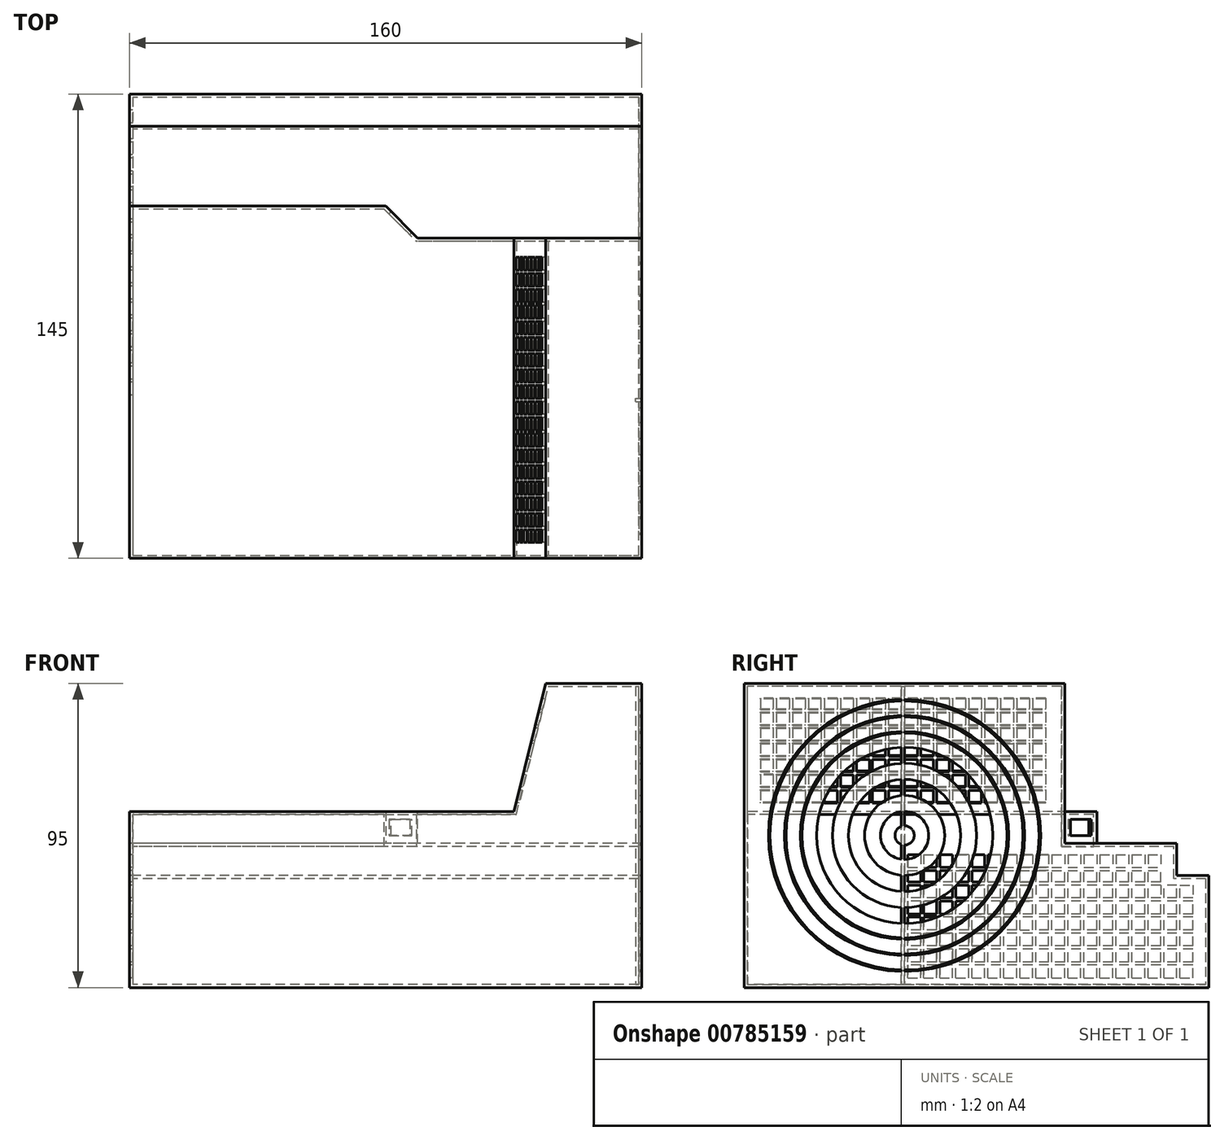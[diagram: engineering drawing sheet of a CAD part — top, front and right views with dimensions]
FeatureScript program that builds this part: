
annotation { "Feature Type Name" : "Feature", "Feature Type Description" : "" }
export const myFeature = defineFeature(function(context is Context, id is Id, definition is map)
    precondition{}
    {
        {
            var Q0;
            Q0=qCreatedBy(makeId("Top.planeOp"),FACE);
            var sketch = newSketch(context, id + "F0", { "sketchPlane" : qUnion([Q0])});
            skLineSegment(sketch, "E0", {"start": v(0, 0) * mm, "end": v(160, 0) * mm});
            skLineSegment(sketch, "E1", {"start": v(160, 0) * mm, "end": v(160, 145) * mm});
            skLineSegment(sketch, "E2", {"start": v(160, 145) * mm, "end": v(0, 145) * mm});
            skLineSegment(sketch, "E3", {"start": v(0, 145) * mm, "end": v(0, 0) * mm});
            skSolve(sketch);
        }
        {
            var Q0;
            Q0=qSketchRegion(id+"F0",true);
            extrude(context, id + "F1", {"entities" : qUnion([Q0]), "depth" : 55 * mm, "offsetDistance" : 25 * mm});
        }
        {
            var Q0;
            Q0=makeQuery(id+"F1.opExtrude","SWEPT_FACE",FACE,{"disambiguationData":[OSD([sQuery(id+"F0.wireOp",EDGE,"E3")])]});
            var sketch = newSketch(context, id + "F2", { "sketchPlane" : qUnion([Q0])});
            skLineSegment(sketch, "E4", {"start": v(-145, 0) * mm, "end": v(-145, 35) * mm});
            skLineSegment(sketch, "E5", {"start": v(-145, 35) * mm, "end": v(-135, 35) * mm});
            skLineSegment(sketch, "E6", {"start": v(-135, 35) * mm, "end": v(-135, 45) * mm});
            skLineSegment(sketch, "E7", {"start": v(-135, 45) * mm, "end": v(-100, 45) * mm});
            skLineSegment(sketch, "E8", {"start": v(-100, 45) * mm, "end": v(-100, 55) * mm});
            skLineSegment(sketch, "E9", {"start": v(-100, 55) * mm, "end": v(-145, 55) * mm});
            skLineSegment(sketch, "E10", {"start": v(-145, 55) * mm, "end": v(-145, 35) * mm});
            skSolve(sketch);
        }
        {
            var Q0;
            Q0=qSketchRegion(id+"F2",true);
            extrude(context, id + "F3", {"entities" : qUnion([Q0]), "operationType" : NewBodyOperationType.REMOVE, "oppositeDirection" : true, "depth" : 165 * mm, "offsetDistance" : 25 * mm});
        }
        {
            var Q0;
            Q0=makeQuery(id+"F1.opExtrude","SWEPT_FACE",FACE,{"disambiguationData":[OSD([sQuery(id+"F0.wireOp",EDGE,"E0")])]});
            var sketch = newSketch(context, id + "F4", { "sketchPlane" : qUnion([Q0])});
            skLineSegment(sketch, "E11", {"start": v(160, 55) * mm, "end": v(120, 55) * mm});
            skLineSegment(sketch, "E12", {"start": v(160, 55) * mm, "end": v(160, 95) * mm});
            skLineSegment(sketch, "E13", {"start": v(160, 95) * mm, "end": v(130, 95) * mm});
            skLineSegment(sketch, "E14", {"start": v(130, 95) * mm, "end": v(120, 55) * mm});
            skSolve(sketch);
        }
        {
            var Q0;
            Q0=qSketchRegion(id+"F4",true);
            extrude(context, id + "F5", {"entities" : qUnion([Q0]), "operationType" : NewBodyOperationType.ADD, "oppositeDirection" : true, "depth" : 100 * mm, "offsetDistance" : 25 * mm});
        }
        {
            var Q0;
            Q0=makeQuery(id+"F1.opExtrude","SWEPT_FACE",FACE,{"disambiguationData":[OSD([sQuery(id+"F0.wireOp",EDGE,"E3")])]});
            var sketch = newSketch(context, id + "F6", { "sketchPlane" : qUnion([Q0])});
            skLineSegment(sketch, "E15.bottom", {"start": v(-100, 45) * mm, "end": v(-110, 45) * mm});
            skLineSegment(sketch, "E15.top", {"start": v(-100, 55) * mm, "end": v(-110, 55) * mm});
            skLineSegment(sketch, "E15.left", {"start": v(-100, 45) * mm, "end": v(-100, 55) * mm});
            skLineSegment(sketch, "E15.right", {"start": v(-110, 45) * mm, "end": v(-110, 55) * mm});
            skSolve(sketch);
        }
        {
            var Q0;
            Q0=qSketchRegion(id+"F6",true);
            extrude(context, id + "F7", {"entities" : qUnion([Q0]), "operationType" : NewBodyOperationType.ADD, "oppositeDirection" : true, "depth" : 90 * mm, "offsetDistance" : 25 * mm});
        }
        {
            var Q0;
            Q0=makeQuery(id+"F7.opExtrude","CAP_EDGE",EDGE,{"disambiguationData":[OSD([sQuery(id+"F6.wireOp",EDGE,"E15.right")])],"isStart":false});
            chamfer(context, id + "F8", {"entities" : qUnion([Q0]), "width" : 10 * mm, "tangentPropagation" : true});
        }
        {
            var Q0;
            Q0=makeQuery(id+"F5.boolean.opBoolean","MERGE",FACE,{"derivedFrom":[makeQuery(id+"F1.opExtrude","SWEPT_FACE",FACE,{"disambiguationData":[OSD([sQuery(id+"F0.wireOp",EDGE,"E0")])]}),makeQuery(id+"F5.opExtrude","CAP_FACE",FACE,{"disambiguationData":[OSD([sQuery(id+"F4.wireOp",EDGE,"E11"),sQuery(id+"F4.wireOp",EDGE,"E12"),sQuery(id+"F4.wireOp",EDGE,"E13"),sQuery(id+"F4.wireOp",EDGE,"E14")])],"isStart":true})]});
            shell(context, id + "F9", {"entities" : qUnion([Q0]), "thickness" : 1 * mm});
        }
        {
            var Q0;
            Q0=makeQuery(id+"F5.opExtrude","SWEPT_FACE",FACE,{"disambiguationData":[OSD([sQuery(id+"F4.wireOp",EDGE,"E14")])]});
            var sketch = newSketch(context, id + "F10", { "sketchPlane" : qUnion([Q0])});
            skLineSegment(sketch, "E16", {"start": v(-94.5, 119.96) * mm, "end": v(-94, 119.96) * mm});
            skLineSegment(sketch, "E17", {"start": v(-89.5, 119.96) * mm, "end": v(-89, 119.96) * mm});
            skLineSegment(sketch, "E18", {"start": v(-4.5, 115.46) * mm, "end": v(-4.5, 114.96) * mm});
            skLineSegment(sketch, "E19", {"start": v(-4.5, 104.96) * mm, "end": v(-4.5, 104.46) * mm});
            skLineSegment(sketch, "E20", {"start": v(-4.5, 99.96) * mm, "end": v(-4.5, 99.46) * mm});
            skLineSegment(sketch, "E21", {"start": v(-4.5, 94.96) * mm, "end": v(-4.5, 94.46) * mm});
            skLineSegment(sketch, "E22.0", {"start": v(-90, 118.96) * mm, "end": v(-90, 115.46) * mm});
            skLineSegment(sketch, "E23.0", {"start": v(-89, 118.96) * mm, "end": v(-89, 115.46) * mm});
            skLineSegment(sketch, "E24.0", {"start": v(-94, 118.96) * mm, "end": v(-94, 115.46) * mm});
            skLineSegment(sketch, "E25.0", {"start": v(-94, 85.46) * mm, "end": v(-90, 85.46) * mm});
            skLineSegment(sketch, "E26.0", {"start": v(-5, 90.46) * mm, "end": v(-9, 90.46) * mm});
            skLineSegment(sketch, "E27.0", {"start": v(-5, 89.46) * mm, "end": v(-9, 89.46) * mm});
            skLineSegment(sketch, "E28.0", {"start": v(-5, 95.46) * mm, "end": v(-9, 95.46) * mm});
            skLineSegment(sketch, "E29.0", {"start": v(-5, 100.46) * mm, "end": v(-9, 100.46) * mm});
            skLineSegment(sketch, "E30.0", {"start": v(-5, 99.46) * mm, "end": v(-9, 99.46) * mm});
            skLineSegment(sketch, "E31.0", {"start": v(-5, 105.46) * mm, "end": v(-9, 105.46) * mm});
            skLineSegment(sketch, "E32.0", {"start": v(-5, 104.46) * mm, "end": v(-9, 104.46) * mm});
            skLineSegment(sketch, "E33.0", {"start": v(-5, 110.46) * mm, "end": v(-9, 110.46) * mm});
            skLineSegment(sketch, "E34.0", {"start": v(-5, 109.46) * mm, "end": v(-9, 109.46) * mm});
            skLineSegment(sketch, "E35.0", {"start": v(-5, 115.46) * mm, "end": v(-9, 115.46) * mm});
            skLineSegment(sketch, "E36.0", {"start": v(-5, 114.46) * mm, "end": v(-9, 114.46) * mm});
            skLineSegment(sketch, "E37.0", {"start": v(-85, 118.96) * mm, "end": v(-85, 115.46) * mm});
            skLineSegment(sketch, "E38.0", {"start": v(-84, 118.96) * mm, "end": v(-84, 115.46) * mm});
            skLineSegment(sketch, "E39.0", {"start": v(-80, 118.96) * mm, "end": v(-80, 115.46) * mm});
            skLineSegment(sketch, "E40.0", {"start": v(-75, 118.96) * mm, "end": v(-75, 115.46) * mm});
            skLineSegment(sketch, "E41.0", {"start": v(-74, 118.96) * mm, "end": v(-74, 115.46) * mm});
            skLineSegment(sketch, "E42.0", {"start": v(-70, 118.96) * mm, "end": v(-70, 115.46) * mm});
            skLineSegment(sketch, "E43.0", {"start": v(-69, 118.96) * mm, "end": v(-69, 115.46) * mm});
            skLineSegment(sketch, "E44.0", {"start": v(-65, 118.96) * mm, "end": v(-65, 115.46) * mm});
            skLineSegment(sketch, "E45.0", {"start": v(-64, 118.96) * mm, "end": v(-64, 115.46) * mm});
            skLineSegment(sketch, "E46.0", {"start": v(-60, 118.96) * mm, "end": v(-60, 115.46) * mm});
            skLineSegment(sketch, "E47.0", {"start": v(-59, 118.96) * mm, "end": v(-59, 115.46) * mm});
            skLineSegment(sketch, "E48.0", {"start": v(-55, 118.96) * mm, "end": v(-55, 115.46) * mm});
            skLineSegment(sketch, "E49.0", {"start": v(-54, 118.96) * mm, "end": v(-54, 115.46) * mm});
            skLineSegment(sketch, "E50.0", {"start": v(-50, 118.96) * mm, "end": v(-50, 115.46) * mm});
            skLineSegment(sketch, "E51.0", {"start": v(-49, 118.96) * mm, "end": v(-49, 115.46) * mm});
            skLineSegment(sketch, "E52.0", {"start": v(-45, 118.96) * mm, "end": v(-45, 115.46) * mm});
            skLineSegment(sketch, "E53.0", {"start": v(-44, 118.96) * mm, "end": v(-44, 115.46) * mm});
            skLineSegment(sketch, "E54.0", {"start": v(-40, 118.96) * mm, "end": v(-40, 115.46) * mm});
            skLineSegment(sketch, "E55.0", {"start": v(-39, 118.96) * mm, "end": v(-39, 115.46) * mm});
            skLineSegment(sketch, "E56.0", {"start": v(-35, 118.96) * mm, "end": v(-35, 115.46) * mm});
            skLineSegment(sketch, "E57.0", {"start": v(-34, 118.96) * mm, "end": v(-34, 115.46) * mm});
            skLineSegment(sketch, "E58.0", {"start": v(-30, 118.96) * mm, "end": v(-30, 115.46) * mm});
            skLineSegment(sketch, "E59.0", {"start": v(-29, 118.96) * mm, "end": v(-29, 115.46) * mm});
            skLineSegment(sketch, "E60.0", {"start": v(-19, 118.96) * mm, "end": v(-19, 115.46) * mm});
            skLineSegment(sketch, "E61.0", {"start": v(-15, 118.96) * mm, "end": v(-15, 115.46) * mm});
            skLineSegment(sketch, "E62.0", {"start": v(-14, 118.96) * mm, "end": v(-14, 115.46) * mm});
            skLineSegment(sketch, "E63.0", {"start": v(-9, 118.96) * mm, "end": v(-9, 115.46) * mm});
            skLineSegment(sketch, "E64.trimOffspring", {"start": v(-4.5, 105.46) * mm, "end": v(-4.5, 104.96) * mm});
            skLineSegment(sketch, "E65.trimOffspring", {"start": v(-4.5, 100.46) * mm, "end": v(-4.5, 99.96) * mm});
            skLineSegment(sketch, "E66.trimOffspring", {"start": v(-4.5, 95.46) * mm, "end": v(-4.5, 94.96) * mm});
            skLineSegment(sketch, "E67.0", {"start": v(-5, 118.96) * mm, "end": v(-5, 115.46) * mm});
            skLineSegment(sketch, "E68.trimOffspring", {"start": v(-85, 119.96) * mm, "end": v(-84.5, 119.96) * mm});
            skLineSegment(sketch, "E69.trimOffspring", {"start": v(-90, 119.96) * mm, "end": v(-89.5, 119.96) * mm});
            skLineSegment(sketch, "E70.trimOffspring", {"start": v(-94, 119.96) * mm, "end": v(-94.5, 119.96) * mm});
            skLineSegment(sketch, "E71.trimOffspring", {"start": v(-89, 119.96) * mm, "end": v(-90, 119.96) * mm});
            skLineSegment(sketch, "E72.0", {"start": v(-94, 118.96) * mm, "end": v(-90, 118.96) * mm});
            skPoint(sketch, "E73.trimOffspring.end.orphan", {"position": v(-98.93, 117.24) * mm});
            skLineSegment(sketch, "E74.trimOffspring", {"start": v(-94, 114.46) * mm, "end": v(-94, 110.46) * mm});
            skLineSegment(sketch, "E75.trimOffspring", {"start": v(-89, 118.96) * mm, "end": v(-85, 118.96) * mm});
            skLineSegment(sketch, "E76.trimOffspring", {"start": v(-84, 118.96) * mm, "end": v(-80, 118.96) * mm});
            skLineSegment(sketch, "E77.trimOffspring", {"start": v(-79, 118.96) * mm, "end": v(-75, 118.96) * mm});
            skLineSegment(sketch, "E78.trimOffspring", {"start": v(-75, 115.46) * mm, "end": v(-79, 115.46) * mm});
            skLineSegment(sketch, "E79.trimOffspring", {"start": v(-74, 114.46) * mm, "end": v(-74, 110.46) * mm});
            skLineSegment(sketch, "E80.trimOffspring", {"start": v(-75, 114.46) * mm, "end": v(-75, 110.46) * mm});
            skLineSegment(sketch, "E81.trimOffspring", {"start": v(-75, 114.46) * mm, "end": v(-79, 114.46) * mm});
            skLineSegment(sketch, "E82.trimOffspring", {"start": v(-79, 114.46) * mm, "end": v(-79, 110.46) * mm});
            skLineSegment(sketch, "E83.trimOffspring", {"start": v(-80, 114.46) * mm, "end": v(-80, 110.46) * mm});
            skLineSegment(sketch, "E84.trimOffspring", {"start": v(-80, 114.46) * mm, "end": v(-84, 114.46) * mm});
            skLineSegment(sketch, "E85.trimOffspring", {"start": v(-74, 118.96) * mm, "end": v(-70, 118.96) * mm});
            skLineSegment(sketch, "E86.trimOffspring", {"start": v(-69, 118.96) * mm, "end": v(-65, 118.96) * mm});
            skLineSegment(sketch, "E87", {"start": v(-79, 118.96) * mm, "end": v(-80, 118.96) * mm});
            skLineSegment(sketch, "E88.trimOffspring", {"start": v(-85, 115.46) * mm, "end": v(-89, 115.46) * mm});
            skLineSegment(sketch, "E89.trimOffspring", {"start": v(-84, 114.46) * mm, "end": v(-84, 110.46) * mm});
            skLineSegment(sketch, "E90.trimOffspring", {"start": v(-85, 114.46) * mm, "end": v(-85, 110.46) * mm});
            skLineSegment(sketch, "E91.trimOffspring", {"start": v(-85, 114.46) * mm, "end": v(-89, 114.46) * mm});
            skLineSegment(sketch, "E92.trimOffspring", {"start": v(-85, 110.46) * mm, "end": v(-89, 110.46) * mm});
            skLineSegment(sketch, "E93.trimOffspring", {"start": v(-84, 109.46) * mm, "end": v(-84, 105.46) * mm});
            skLineSegment(sketch, "E94.trimOffspring", {"start": v(-85, 109.46) * mm, "end": v(-85, 105.46) * mm});
            skLineSegment(sketch, "E95.trimOffspring", {"start": v(-85, 109.46) * mm, "end": v(-89, 109.46) * mm});
            skLineSegment(sketch, "E96.trimOffspring", {"start": v(-90, 109.46) * mm, "end": v(-90, 105.46) * mm});
            skLineSegment(sketch, "E97.trimOffspring", {"start": v(-89, 109.46) * mm, "end": v(-89, 105.46) * mm});
            skLineSegment(sketch, "E98.trimOffspring", {"start": v(-90, 110.46) * mm, "end": v(-94, 110.46) * mm});
            skLineSegment(sketch, "E99.trimOffspring", {"start": v(-90, 109.46) * mm, "end": v(-94, 109.46) * mm});
            skLineSegment(sketch, "E100.trimOffspring", {"start": v(-90, 114.46) * mm, "end": v(-94, 114.46) * mm});
            skLineSegment(sketch, "E101.trimOffspring", {"start": v(-89, 114.46) * mm, "end": v(-89, 110.46) * mm});
            skLineSegment(sketch, "E102.trimOffspring", {"start": v(-90, 114.46) * mm, "end": v(-90, 110.46) * mm});
            skLineSegment(sketch, "E103.trimOffspring", {"start": v(-90, 115.46) * mm, "end": v(-94, 115.46) * mm});
            skLineSegment(sketch, "E104.trimOffspring", {"start": v(-80, 109.46) * mm, "end": v(-80, 105.46) * mm});
            skLineSegment(sketch, "E105.trimOffspring", {"start": v(-80, 110.46) * mm, "end": v(-84, 110.46) * mm});
            skLineSegment(sketch, "E106.trimOffspring", {"start": v(-79, 109.46) * mm, "end": v(-79, 105.46) * mm});
            skLineSegment(sketch, "E107.trimOffspring", {"start": v(-80, 109.46) * mm, "end": v(-84, 109.46) * mm});
            skLineSegment(sketch, "E108.trimOffspring", {"start": v(-75, 109.46) * mm, "end": v(-79, 109.46) * mm});
            skLineSegment(sketch, "E109.trimOffspring", {"start": v(-74, 109.46) * mm, "end": v(-74, 105.46) * mm});
            skLineSegment(sketch, "E110.trimOffspring", {"start": v(-75, 109.46) * mm, "end": v(-75, 105.46) * mm});
            skLineSegment(sketch, "E111.trimOffspring", {"start": v(-75, 110.46) * mm, "end": v(-79, 110.46) * mm});
            skLineSegment(sketch, "E112.trimOffspring", {"start": v(-70, 109.46) * mm, "end": v(-70, 105.46) * mm});
            skLineSegment(sketch, "E113.trimOffspring", {"start": v(-70, 110.46) * mm, "end": v(-74, 110.46) * mm});
            skLineSegment(sketch, "E114.trimOffspring", {"start": v(-69, 109.46) * mm, "end": v(-69, 105.46) * mm});
            skLineSegment(sketch, "E115.trimOffspring", {"start": v(-70, 109.46) * mm, "end": v(-74, 109.46) * mm});
            skLineSegment(sketch, "E116.trimOffspring", {"start": v(-70, 114.46) * mm, "end": v(-74, 114.46) * mm});
            skLineSegment(sketch, "E117.trimOffspring", {"start": v(-70, 114.46) * mm, "end": v(-70, 110.46) * mm});
            skLineSegment(sketch, "E118.trimOffspring", {"start": v(-70, 115.46) * mm, "end": v(-74, 115.46) * mm});
            skLineSegment(sketch, "E119.trimOffspring", {"start": v(-69, 114.46) * mm, "end": v(-69, 110.46) * mm});
            skLineSegment(sketch, "E120.trimOffspring", {"start": v(-65, 114.46) * mm, "end": v(-65, 110.46) * mm});
            skLineSegment(sketch, "E121.trimOffspring", {"start": v(-65, 115.46) * mm, "end": v(-69, 115.46) * mm});
            skLineSegment(sketch, "E122.trimOffspring", {"start": v(-64, 118.96) * mm, "end": v(-60, 118.96) * mm});
            skLineSegment(sketch, "E123.trimOffspring", {"start": v(-65, 114.46) * mm, "end": v(-69, 114.46) * mm});
            skLineSegment(sketch, "E124.trimOffspring", {"start": v(-64, 114.46) * mm, "end": v(-64, 110.46) * mm});
            skLineSegment(sketch, "E125.trimOffspring", {"start": v(-59, 118.96) * mm, "end": v(-55, 118.96) * mm});
            skLineSegment(sketch, "E126.trimOffspring", {"start": v(-60, 115.46) * mm, "end": v(-64, 115.46) * mm});
            skLineSegment(sketch, "E127.trimOffspring", {"start": v(-60, 114.46) * mm, "end": v(-60, 110.46) * mm});
            skLineSegment(sketch, "E128.trimOffspring", {"start": v(-60, 114.46) * mm, "end": v(-64, 114.46) * mm});
            skLineSegment(sketch, "E129.trimOffspring", {"start": v(-59, 114.46) * mm, "end": v(-59, 110.46) * mm});
            skLineSegment(sketch, "E130.trimOffspring", {"start": v(-60, 110.46) * mm, "end": v(-64, 110.46) * mm});
            skLineSegment(sketch, "E131.trimOffspring", {"start": v(-60, 109.46) * mm, "end": v(-60, 105.46) * mm});
            skLineSegment(sketch, "E132.trimOffspring", {"start": v(-60, 109.46) * mm, "end": v(-64, 109.46) * mm});
            skLineSegment(sketch, "E133.trimOffspring", {"start": v(-59, 109.46) * mm, "end": v(-59, 105.46) * mm});
            skLineSegment(sketch, "E134.trimOffspring", {"start": v(-64, 109.46) * mm, "end": v(-64, 105.46) * mm});
            skLineSegment(sketch, "E135.trimOffspring", {"start": v(-65, 110.46) * mm, "end": v(-69, 110.46) * mm});
            skLineSegment(sketch, "E136.trimOffspring", {"start": v(-65, 109.46) * mm, "end": v(-65, 105.46) * mm});
            skLineSegment(sketch, "E137.trimOffspring", {"start": v(-65, 109.46) * mm, "end": v(-69, 109.46) * mm});
            skLineSegment(sketch, "E138.trimOffspring", {"start": v(-94, 109.46) * mm, "end": v(-94, 105.46) * mm});
            skLineSegment(sketch, "E139.trimOffspring", {"start": v(-94, 99.46) * mm, "end": v(-94, 95.46) * mm});
            skLineSegment(sketch, "E140.trimOffspring", {"start": v(-90, 99.46) * mm, "end": v(-90, 95.46) * mm});
            skLineSegment(sketch, "E141.trimOffspring", {"start": v(-90, 100.46) * mm, "end": v(-94, 100.46) * mm});
            skLineSegment(sketch, "E142.trimOffspring", {"start": v(-89, 99.46) * mm, "end": v(-89, 95.46) * mm});
            skLineSegment(sketch, "E143.trimOffspring", {"start": v(-90, 99.46) * mm, "end": v(-94, 99.46) * mm});
            skLineSegment(sketch, "E144.trimOffspring", {"start": v(-90, 104.46) * mm, "end": v(-94, 104.46) * mm});
            skLineSegment(sketch, "E145.trimOffspring", {"start": v(-90, 104.46) * mm, "end": v(-90, 100.46) * mm});
            skLineSegment(sketch, "E146.trimOffspring", {"start": v(-90, 105.46) * mm, "end": v(-94, 105.46) * mm});
            skLineSegment(sketch, "E147.trimOffspring", {"start": v(-89, 104.46) * mm, "end": v(-89, 100.46) * mm});
            skLineSegment(sketch, "E148.trimOffspring", {"start": v(-84, 104.46) * mm, "end": v(-84, 100.46) * mm});
            skLineSegment(sketch, "E149.trimOffspring", {"start": v(-85, 105.46) * mm, "end": v(-89, 105.46) * mm});
            skLineSegment(sketch, "E150.trimOffspring", {"start": v(-85, 104.46) * mm, "end": v(-85, 100.46) * mm});
            skLineSegment(sketch, "E151.trimOffspring", {"start": v(-85, 104.46) * mm, "end": v(-89, 104.46) * mm});
            skLineSegment(sketch, "E152.trimOffspring", {"start": v(-80, 104.46) * mm, "end": v(-80, 100.46) * mm});
            skLineSegment(sketch, "E153.trimOffspring", {"start": v(-80, 105.46) * mm, "end": v(-84, 105.46) * mm});
            skLineSegment(sketch, "E154.trimOffspring", {"start": v(-79, 104.46) * mm, "end": v(-79, 100.46) * mm});
            skLineSegment(sketch, "E155.trimOffspring", {"start": v(-80, 104.46) * mm, "end": v(-84, 104.46) * mm});
            skLineSegment(sketch, "E156", {"start": v(-79, 118.96) * mm, "end": v(-79, 115.46) * mm});
            skLineSegment(sketch, "E157.trimOffspring", {"start": v(-80, 115.46) * mm, "end": v(-84, 115.46) * mm});
            skLineSegment(sketch, "E158.trimOffspring", {"start": v(-70, 105.46) * mm, "end": v(-74, 105.46) * mm});
            skLineSegment(sketch, "E159.trimOffspring", {"start": v(-70, 104.46) * mm, "end": v(-74, 104.46) * mm});
            skLineSegment(sketch, "E160.trimOffspring", {"start": v(-69, 104.46) * mm, "end": v(-69, 100.46) * mm});
            skLineSegment(sketch, "E161.trimOffspring", {"start": v(-70, 104.46) * mm, "end": v(-70, 100.46) * mm});
            skLineSegment(sketch, "E162.trimOffspring", {"start": v(-74, 104.46) * mm, "end": v(-74, 100.46) * mm});
            skLineSegment(sketch, "E163.trimOffspring", {"start": v(-75, 104.46) * mm, "end": v(-79, 104.46) * mm});
            skLineSegment(sketch, "E164.trimOffspring", {"start": v(-75, 104.46) * mm, "end": v(-75, 100.46) * mm});
            skLineSegment(sketch, "E165.trimOffspring", {"start": v(-75, 105.46) * mm, "end": v(-79, 105.46) * mm});
            skLineSegment(sketch, "E166.trimOffspring", {"start": v(-94, 94.46) * mm, "end": v(-94, 90.46) * mm});
            skLineSegment(sketch, "E167.trimOffspring", {"start": v(-90, 94.46) * mm, "end": v(-90, 90.46) * mm});
            skLineSegment(sketch, "E168.trimOffspring", {"start": v(-89, 94.46) * mm, "end": v(-89, 90.46) * mm});
            skLineSegment(sketch, "E169.trimOffspring", {"start": v(-90, 95.46) * mm, "end": v(-94, 95.46) * mm});
            skLineSegment(sketch, "E170.trimOffspring", {"start": v(-94, 89.46) * mm, "end": v(-94, 85.46) * mm});
            skLineSegment(sketch, "E171.trimOffspring", {"start": v(-89, 85.46) * mm, "end": v(-85, 85.46) * mm});
            skLineSegment(sketch, "E172.trimOffspring", {"start": v(-90, 89.46) * mm, "end": v(-94, 89.46) * mm});
            skLineSegment(sketch, "E173.trimOffspring", {"start": v(-90, 90.46) * mm, "end": v(-94, 90.46) * mm});
            skLineSegment(sketch, "E174.trimOffspring", {"start": v(-90, 89.46) * mm, "end": v(-90, 85.46) * mm});
            skLineSegment(sketch, "E175.trimOffspring", {"start": v(-89, 89.46) * mm, "end": v(-89, 85.46) * mm});
            skLineSegment(sketch, "E176.trimOffspring", {"start": v(-90, 94.46) * mm, "end": v(-94, 94.46) * mm});
            skLineSegment(sketch, "E177.trimOffspring", {"start": v(-85, 94.46) * mm, "end": v(-89, 94.46) * mm});
            skLineSegment(sketch, "E178.trimOffspring", {"start": v(-85, 94.46) * mm, "end": v(-85, 90.46) * mm});
            skLineSegment(sketch, "E179.trimOffspring", {"start": v(-85, 95.46) * mm, "end": v(-89, 95.46) * mm});
            skLineSegment(sketch, "E180.trimOffspring", {"start": v(-84, 94.46) * mm, "end": v(-84, 90.46) * mm});
            skLineSegment(sketch, "E181.trimOffspring", {"start": v(-85, 99.46) * mm, "end": v(-89, 99.46) * mm});
            skLineSegment(sketch, "E182.trimOffspring", {"start": v(-85, 99.46) * mm, "end": v(-85, 95.46) * mm});
            skLineSegment(sketch, "E183.trimOffspring", {"start": v(-85, 100.46) * mm, "end": v(-89, 100.46) * mm});
            skLineSegment(sketch, "E184.trimOffspring", {"start": v(-84, 99.46) * mm, "end": v(-84, 95.46) * mm});
            skLineSegment(sketch, "E185.trimOffspring", {"start": v(-80, 99.46) * mm, "end": v(-80, 95.46) * mm});
            skLineSegment(sketch, "E186.trimOffspring", {"start": v(-80, 99.46) * mm, "end": v(-84, 99.46) * mm});
            skLineSegment(sketch, "E187.trimOffspring", {"start": v(-79, 99.46) * mm, "end": v(-79, 95.46) * mm});
            skLineSegment(sketch, "E188.trimOffspring", {"start": v(-80, 100.46) * mm, "end": v(-84, 100.46) * mm});
            skLineSegment(sketch, "E189.trimOffspring", {"start": v(-75, 100.46) * mm, "end": v(-79, 100.46) * mm});
            skLineSegment(sketch, "E190.trimOffspring", {"start": v(-75, 99.46) * mm, "end": v(-75, 95.46) * mm});
            skLineSegment(sketch, "E191.trimOffspring", {"start": v(-75, 99.46) * mm, "end": v(-79, 99.46) * mm});
            skLineSegment(sketch, "E192.trimOffspring", {"start": v(-74, 99.46) * mm, "end": v(-74, 95.46) * mm});
            skLineSegment(sketch, "E193.trimOffspring", {"start": v(-70, 99.46) * mm, "end": v(-70, 95.46) * mm});
            skLineSegment(sketch, "E194.trimOffspring", {"start": v(-70, 99.46) * mm, "end": v(-74, 99.46) * mm});
            skLineSegment(sketch, "E195.trimOffspring", {"start": v(-69, 99.46) * mm, "end": v(-69, 95.46) * mm});
            skLineSegment(sketch, "E196.trimOffspring", {"start": v(-70, 100.46) * mm, "end": v(-74, 100.46) * mm});
            skLineSegment(sketch, "E197.trimOffspring", {"start": v(-65, 105.46) * mm, "end": v(-69, 105.46) * mm});
            skLineSegment(sketch, "E198.trimOffspring", {"start": v(-65, 104.46) * mm, "end": v(-69, 104.46) * mm});
            skLineSegment(sketch, "E199.trimOffspring", {"start": v(-64, 104.46) * mm, "end": v(-64, 100.46) * mm});
            skLineSegment(sketch, "E200.trimOffspring", {"start": v(-65, 104.46) * mm, "end": v(-65, 100.46) * mm});
            skLineSegment(sketch, "E201.trimOffspring", {"start": v(-60, 104.46) * mm, "end": v(-60, 100.46) * mm});
            skLineSegment(sketch, "E202.trimOffspring", {"start": v(-59, 104.46) * mm, "end": v(-59, 100.46) * mm});
            skLineSegment(sketch, "E203.trimOffspring", {"start": v(-60, 105.46) * mm, "end": v(-64, 105.46) * mm});
            skLineSegment(sketch, "E204.trimOffspring", {"start": v(-60, 104.46) * mm, "end": v(-64, 104.46) * mm});
            skLineSegment(sketch, "E205.trimOffspring", {"start": v(-55, 104.46) * mm, "end": v(-59, 104.46) * mm});
            skLineSegment(sketch, "E206.trimOffspring", {"start": v(-55, 104.46) * mm, "end": v(-55, 100.46) * mm});
            skLineSegment(sketch, "E207.trimOffspring", {"start": v(-55, 105.46) * mm, "end": v(-59, 105.46) * mm});
            skLineSegment(sketch, "E208.trimOffspring", {"start": v(-54, 104.46) * mm, "end": v(-54, 100.46) * mm});
            skLineSegment(sketch, "E209.trimOffspring", {"start": v(-55, 109.46) * mm, "end": v(-59, 109.46) * mm});
            skLineSegment(sketch, "E210.trimOffspring", {"start": v(-55, 109.46) * mm, "end": v(-55, 105.46) * mm});
            skLineSegment(sketch, "E211.trimOffspring", {"start": v(-55, 110.46) * mm, "end": v(-59, 110.46) * mm});
            skLineSegment(sketch, "E212.trimOffspring", {"start": v(-54, 109.46) * mm, "end": v(-54, 105.46) * mm});
            skLineSegment(sketch, "E213.trimOffspring", {"start": v(-55, 114.46) * mm, "end": v(-59, 114.46) * mm});
            skLineSegment(sketch, "E214.trimOffspring", {"start": v(-55, 115.46) * mm, "end": v(-59, 115.46) * mm});
            skLineSegment(sketch, "E215.trimOffspring", {"start": v(-55, 114.46) * mm, "end": v(-55, 110.46) * mm});
            skLineSegment(sketch, "E216.trimOffspring", {"start": v(-54, 114.46) * mm, "end": v(-54, 110.46) * mm});
            skLineSegment(sketch, "E217.trimOffspring", {"start": v(-85, 89.46) * mm, "end": v(-89, 89.46) * mm});
            skLineSegment(sketch, "E218.trimOffspring", {"start": v(-85, 90.46) * mm, "end": v(-89, 90.46) * mm});
            skLineSegment(sketch, "E219.trimOffspring", {"start": v(-85, 89.46) * mm, "end": v(-85, 85.46) * mm});
            skLineSegment(sketch, "E220.trimOffspring", {"start": v(-84, 89.46) * mm, "end": v(-84, 85.46) * mm});
            skLineSegment(sketch, "E221.trimOffspring", {"start": v(-80, 89.46) * mm, "end": v(-84, 89.46) * mm});
            skLineSegment(sketch, "E222.trimOffspring", {"start": v(-80, 90.46) * mm, "end": v(-84, 90.46) * mm});
            skLineSegment(sketch, "E223.trimOffspring", {"start": v(-79, 89.46) * mm, "end": v(-79, 85.46) * mm});
            skLineSegment(sketch, "E224.trimOffspring", {"start": v(-80, 89.46) * mm, "end": v(-80, 85.46) * mm});
            skLineSegment(sketch, "E225.trimOffspring", {"start": v(-80, 94.46) * mm, "end": v(-84, 94.46) * mm});
            skLineSegment(sketch, "E226.trimOffspring", {"start": v(-80, 95.46) * mm, "end": v(-84, 95.46) * mm});
            skLineSegment(sketch, "E227.trimOffspring", {"start": v(-79, 94.46) * mm, "end": v(-79, 90.46) * mm});
            skLineSegment(sketch, "E228.trimOffspring", {"start": v(-80, 94.46) * mm, "end": v(-80, 90.46) * mm});
            skLineSegment(sketch, "E229.trimOffspring", {"start": v(-75, 94.46) * mm, "end": v(-75, 90.46) * mm});
            skLineSegment(sketch, "E230.trimOffspring", {"start": v(-75, 95.46) * mm, "end": v(-79, 95.46) * mm});
            skLineSegment(sketch, "E231.trimOffspring", {"start": v(-75, 94.46) * mm, "end": v(-79, 94.46) * mm});
            skLineSegment(sketch, "E232.trimOffspring", {"start": v(-74, 94.46) * mm, "end": v(-74, 90.46) * mm});
            skLineSegment(sketch, "E233.trimOffspring", {"start": v(-75, 89.46) * mm, "end": v(-79, 89.46) * mm});
            skLineSegment(sketch, "E234.trimOffspring", {"start": v(-75, 89.46) * mm, "end": v(-75, 85.46) * mm});
            skLineSegment(sketch, "E235.trimOffspring", {"start": v(-75, 90.46) * mm, "end": v(-79, 90.46) * mm});
            skLineSegment(sketch, "E236.trimOffspring", {"start": v(-74, 89.46) * mm, "end": v(-74, 85.46) * mm});
            skLineSegment(sketch, "E237.trimOffspring", {"start": v(-70, 89.46) * mm, "end": v(-70, 85.46) * mm});
            skLineSegment(sketch, "E238.trimOffspring", {"start": v(-69, 89.46) * mm, "end": v(-69, 85.46) * mm});
            skLineSegment(sketch, "E239.trimOffspring", {"start": v(-70, 90.46) * mm, "end": v(-74, 90.46) * mm});
            skLineSegment(sketch, "E240.trimOffspring", {"start": v(-70, 89.46) * mm, "end": v(-74, 89.46) * mm});
            skLineSegment(sketch, "E241.trimOffspring", {"start": v(-70, 94.46) * mm, "end": v(-74, 94.46) * mm});
            skLineSegment(sketch, "E242.trimOffspring", {"start": v(-70, 94.46) * mm, "end": v(-70, 90.46) * mm});
            skLineSegment(sketch, "E243.trimOffspring", {"start": v(-70, 95.46) * mm, "end": v(-74, 95.46) * mm});
            skLineSegment(sketch, "E244.trimOffspring", {"start": v(-69, 94.46) * mm, "end": v(-69, 90.46) * mm});
            skLineSegment(sketch, "E245.trimOffspring", {"start": v(-65, 94.46) * mm, "end": v(-69, 94.46) * mm});
            skLineSegment(sketch, "E246.trimOffspring", {"start": v(-64, 94.46) * mm, "end": v(-64, 90.46) * mm});
            skLineSegment(sketch, "E247.trimOffspring", {"start": v(-65, 95.46) * mm, "end": v(-69, 95.46) * mm});
            skLineSegment(sketch, "E248.trimOffspring", {"start": v(-65, 94.46) * mm, "end": v(-65, 90.46) * mm});
            skLineSegment(sketch, "E249.trimOffspring", {"start": v(-65, 99.46) * mm, "end": v(-69, 99.46) * mm});
            skLineSegment(sketch, "E250.trimOffspring", {"start": v(-65, 99.46) * mm, "end": v(-65, 95.46) * mm});
            skLineSegment(sketch, "E251.trimOffspring", {"start": v(-65, 100.46) * mm, "end": v(-69, 100.46) * mm});
            skLineSegment(sketch, "E252.trimOffspring", {"start": v(-64, 99.46) * mm, "end": v(-64, 95.46) * mm});
            skLineSegment(sketch, "E253.trimOffspring", {"start": v(-60, 99.46) * mm, "end": v(-60, 95.46) * mm});
            skLineSegment(sketch, "E254.trimOffspring", {"start": v(-60, 99.46) * mm, "end": v(-64, 99.46) * mm});
            skLineSegment(sketch, "E255.trimOffspring", {"start": v(-59, 99.46) * mm, "end": v(-59, 95.46) * mm});
            skLineSegment(sketch, "E256.trimOffspring", {"start": v(-60, 100.46) * mm, "end": v(-64, 100.46) * mm});
            skLineSegment(sketch, "E257.trimOffspring", {"start": v(-54, 85.46) * mm, "end": v(-50, 85.46) * mm});
            skLineSegment(sketch, "E258.trimOffspring", {"start": v(-44, 85.46) * mm, "end": v(-40, 85.46) * mm});
            skLineSegment(sketch, "E259.trimOffspring", {"start": v(-45, 89.46) * mm, "end": v(-49, 89.46) * mm});
            skLineSegment(sketch, "E260.trimOffspring", {"start": v(-45, 90.46) * mm, "end": v(-49, 90.46) * mm});
            skLineSegment(sketch, "E261.trimOffspring", {"start": v(-44, 89.46) * mm, "end": v(-44, 85.46) * mm});
            skLineSegment(sketch, "E262.trimOffspring", {"start": v(-45, 89.46) * mm, "end": v(-45, 85.46) * mm});
            skLineSegment(sketch, "E263.trimOffspring", {"start": v(-50, 90.46) * mm, "end": v(-54, 90.46) * mm});
            skLineSegment(sketch, "E264.trimOffspring", {"start": v(-50, 89.46) * mm, "end": v(-50, 85.46) * mm});
            skLineSegment(sketch, "E265.trimOffspring", {"start": v(-50, 89.46) * mm, "end": v(-54, 89.46) * mm});
            skLineSegment(sketch, "E266.trimOffspring", {"start": v(-54, 89.46) * mm, "end": v(-54, 85.46) * mm});
            skLineSegment(sketch, "E267.trimOffspring", {"start": v(-55, 90.46) * mm, "end": v(-59, 90.46) * mm});
            skLineSegment(sketch, "E268.trimOffspring", {"start": v(-55, 89.46) * mm, "end": v(-55, 85.46) * mm});
            skLineSegment(sketch, "E269.trimOffspring", {"start": v(-55, 89.46) * mm, "end": v(-59, 89.46) * mm});
            skLineSegment(sketch, "E270.trimOffspring", {"start": v(-59, 89.46) * mm, "end": v(-59, 85.46) * mm});
            skLineSegment(sketch, "E271.trimOffspring", {"start": v(-60, 90.46) * mm, "end": v(-64, 90.46) * mm});
            skLineSegment(sketch, "E272.trimOffspring", {"start": v(-60, 89.46) * mm, "end": v(-64, 89.46) * mm});
            skLineSegment(sketch, "E273.trimOffspring", {"start": v(-64, 89.46) * mm, "end": v(-64, 85.46) * mm});
            skLineSegment(sketch, "E274.trimOffspring", {"start": v(-65, 89.46) * mm, "end": v(-65, 85.46) * mm});
            skLineSegment(sketch, "E275.trimOffspring", {"start": v(-65, 89.46) * mm, "end": v(-69, 89.46) * mm});
            skLineSegment(sketch, "E276.trimOffspring", {"start": v(-65, 90.46) * mm, "end": v(-69, 90.46) * mm});
            skLineSegment(sketch, "E277.trimOffspring", {"start": v(-60, 89.46) * mm, "end": v(-60, 85.46) * mm});
            skLineSegment(sketch, "E278.trimOffspring", {"start": v(-59, 85.46) * mm, "end": v(-55, 85.46) * mm});
            skLineSegment(sketch, "E279.trimOffspring", {"start": v(-64, 85.46) * mm, "end": v(-60, 85.46) * mm});
            skLineSegment(sketch, "E280.trimOffspring", {"start": v(-69, 85.46) * mm, "end": v(-65, 85.46) * mm});
            skLineSegment(sketch, "E281.trimOffspring", {"start": v(-74, 85.46) * mm, "end": v(-70, 85.46) * mm});
            skLineSegment(sketch, "E282.trimOffspring", {"start": v(-79, 85.46) * mm, "end": v(-75, 85.46) * mm});
            skLineSegment(sketch, "E283.trimOffspring", {"start": v(-39, 85.46) * mm, "end": v(-35, 85.46) * mm});
            skLineSegment(sketch, "E284.trimOffspring", {"start": v(-40, 89.46) * mm, "end": v(-44, 89.46) * mm});
            skLineSegment(sketch, "E285.trimOffspring", {"start": v(-40, 90.46) * mm, "end": v(-44, 90.46) * mm});
            skLineSegment(sketch, "E286.trimOffspring", {"start": v(-39, 89.46) * mm, "end": v(-39, 85.46) * mm});
            skLineSegment(sketch, "E287.trimOffspring", {"start": v(-40, 89.46) * mm, "end": v(-40, 85.46) * mm});
            skLineSegment(sketch, "E288.trimOffspring", {"start": v(-34, 89.46) * mm, "end": v(-34, 85.46) * mm});
            skLineSegment(sketch, "E289.trimOffspring", {"start": v(-35, 90.46) * mm, "end": v(-39, 90.46) * mm});
            skLineSegment(sketch, "E290.trimOffspring", {"start": v(-35, 89.46) * mm, "end": v(-35, 85.46) * mm});
            skLineSegment(sketch, "E291.trimOffspring", {"start": v(-35, 89.46) * mm, "end": v(-39, 89.46) * mm});
            skLineSegment(sketch, "E292.trimOffspring", {"start": v(-34, 85.46) * mm, "end": v(-30, 85.46) * mm});
            skLineSegment(sketch, "E293.trimOffspring", {"start": v(-29, 85.46) * mm, "end": v(-25, 85.46) * mm});
            skLineSegment(sketch, "E294.trimOffspring", {"start": v(-49, 104.46) * mm, "end": v(-49, 100.46) * mm});
            skLineSegment(sketch, "E295.trimOffspring", {"start": v(-50, 105.46) * mm, "end": v(-54, 105.46) * mm});
            skLineSegment(sketch, "E296.trimOffspring", {"start": v(-50, 104.46) * mm, "end": v(-50, 100.46) * mm});
            skLineSegment(sketch, "E297.trimOffspring", {"start": v(-50, 104.46) * mm, "end": v(-54, 104.46) * mm});
            skLineSegment(sketch, "E298.trimOffspring", {"start": v(-50, 100.46) * mm, "end": v(-54, 100.46) * mm});
            skLineSegment(sketch, "E299.trimOffspring", {"start": v(-49, 99.46) * mm, "end": v(-49, 90.46) * mm});
            skLineSegment(sketch, "E300.trimOffspring", {"start": v(-50, 99.46) * mm, "end": v(-50, 95.46) * mm});
            skLineSegment(sketch, "E301.trimOffspring", {"start": v(-50, 99.46) * mm, "end": v(-54, 99.46) * mm});
            skLineSegment(sketch, "E302.trimOffspring", {"start": v(-54, 99.46) * mm, "end": v(-54, 95.46) * mm});
            skLineSegment(sketch, "E303.trimOffspring", {"start": v(-55, 100.46) * mm, "end": v(-59, 100.46) * mm});
            skLineSegment(sketch, "E304.trimOffspring", {"start": v(-55, 99.46) * mm, "end": v(-55, 95.46) * mm});
            skLineSegment(sketch, "E305.trimOffspring", {"start": v(-55, 99.46) * mm, "end": v(-59, 99.46) * mm});
            skLineSegment(sketch, "E306.trimOffspring", {"start": v(-55, 95.46) * mm, "end": v(-59, 95.46) * mm});
            skLineSegment(sketch, "E307.trimOffspring", {"start": v(-54, 94.46) * mm, "end": v(-54, 90.46) * mm});
            skLineSegment(sketch, "E308.trimOffspring", {"start": v(-55, 94.46) * mm, "end": v(-55, 90.46) * mm});
            skLineSegment(sketch, "E309.trimOffspring", {"start": v(-55, 94.46) * mm, "end": v(-59, 94.46) * mm});
            skLineSegment(sketch, "E310.trimOffspring", {"start": v(-59, 94.46) * mm, "end": v(-59, 90.46) * mm});
            skLineSegment(sketch, "E311.trimOffspring", {"start": v(-60, 95.46) * mm, "end": v(-64, 95.46) * mm});
            skLineSegment(sketch, "E312.trimOffspring", {"start": v(-60, 94.46) * mm, "end": v(-60, 90.46) * mm});
            skLineSegment(sketch, "E313.trimOffspring", {"start": v(-60, 94.46) * mm, "end": v(-64, 94.46) * mm});
            skLineSegment(sketch, "E314.trimOffspring", {"start": v(-45, 99.46) * mm, "end": v(-49, 99.46) * mm});
            skLineSegment(sketch, "E315.trimOffspring", {"start": v(-44, 99.46) * mm, "end": v(-44, 95.46) * mm});
            skLineSegment(sketch, "E316.trimOffspring", {"start": v(-45, 100.46) * mm, "end": v(-49, 100.46) * mm});
            skLineSegment(sketch, "E317.trimOffspring", {"start": v(-45, 99.46) * mm, "end": v(-45, 95.46) * mm});
            skLineSegment(sketch, "E318.trimOffspring", {"start": v(-45, 104.46) * mm, "end": v(-49, 104.46) * mm});
            skLineSegment(sketch, "E319.trimOffspring", {"start": v(-45, 105.46) * mm, "end": v(-49, 105.46) * mm});
            skLineSegment(sketch, "E320.trimOffspring", {"start": v(-44, 104.46) * mm, "end": v(-44, 100.46) * mm});
            skLineSegment(sketch, "E321.trimOffspring", {"start": v(-50, 109.46) * mm, "end": v(-54, 109.46) * mm});
            skLineSegment(sketch, "E322.trimOffspring", {"start": v(-50, 109.46) * mm, "end": v(-50, 105.46) * mm});
            skLineSegment(sketch, "E323.trimOffspring", {"start": v(-50, 110.46) * mm, "end": v(-54, 110.46) * mm});
            skLineSegment(sketch, "E324.trimOffspring", {"start": v(-49, 109.46) * mm, "end": v(-49, 105.46) * mm});
            skLineSegment(sketch, "E325.trimOffspring", {"start": v(-45, 109.46) * mm, "end": v(-45, 105.46) * mm});
            skLineSegment(sketch, "E326.trimOffspring", {"start": v(-45, 109.46) * mm, "end": v(-49, 109.46) * mm});
            skLineSegment(sketch, "E327.trimOffspring", {"start": v(-44, 109.46) * mm, "end": v(-44, 105.46) * mm});
            skLineSegment(sketch, "E328.trimOffspring", {"start": v(-45, 110.46) * mm, "end": v(-49, 110.46) * mm});
            skLineSegment(sketch, "E329", {"start": v(-45, 104.46) * mm, "end": v(-45, 100.46) * mm});
            skLineSegment(sketch, "E330", {"start": v(-44, 100.46) * mm, "end": v(-40, 100.46) * mm});
            skLineSegment(sketch, "E331", {"start": v(-40, 109.46) * mm, "end": v(-44, 109.46) * mm});
            skLineSegment(sketch, "E332.trimOffspring", {"start": v(-39, 99.46) * mm, "end": v(-39, 95.46) * mm});
            skLineSegment(sketch, "E333.trimOffspring", {"start": v(-40, 99.46) * mm, "end": v(-40, 95.46) * mm});
            skLineSegment(sketch, "E334.trimOffspring", {"start": v(-40, 99.46) * mm, "end": v(-44, 99.46) * mm});
            skLineSegment(sketch, "E335.trimOffspring", {"start": v(-40, 104.46) * mm, "end": v(-44, 104.46) * mm});
            skLineSegment(sketch, "E336.trimOffspring", {"start": v(-40, 104.46) * mm, "end": v(-40, 100.46) * mm});
            skLineSegment(sketch, "E337.trimOffspring", {"start": v(-40, 105.46) * mm, "end": v(-44, 105.46) * mm});
            skLineSegment(sketch, "E338.trimOffspring", {"start": v(-39, 104.46) * mm, "end": v(-39, 100.46) * mm});
            skLineSegment(sketch, "E339.trimOffspring", {"start": v(-40, 109.46) * mm, "end": v(-40, 105.46) * mm});
            skLineSegment(sketch, "E340.trimOffspring", {"start": v(-40, 110.46) * mm, "end": v(-44, 110.46) * mm});
            skLineSegment(sketch, "E341.trimOffspring", {"start": v(-39, 109.46) * mm, "end": v(-39, 105.46) * mm});
            skLineSegment(sketch, "E342.trimOffspring", {"start": v(-40, 94.46) * mm, "end": v(-44, 94.46) * mm});
            skLineSegment(sketch, "E343.trimOffspring", {"start": v(-40, 94.46) * mm, "end": v(-40, 90.46) * mm});
            skLineSegment(sketch, "E344.trimOffspring", {"start": v(-40, 95.46) * mm, "end": v(-44, 95.46) * mm});
            skLineSegment(sketch, "E345.trimOffspring", {"start": v(-39, 94.46) * mm, "end": v(-39, 90.46) * mm});
            skLineSegment(sketch, "E346.trimOffspring", {"start": v(-44, 94.46) * mm, "end": v(-44, 90.46) * mm});
            skLineSegment(sketch, "E347.trimOffspring", {"start": v(-45, 95.46) * mm, "end": v(-49, 95.46) * mm});
            skLineSegment(sketch, "E348.trimOffspring", {"start": v(-45, 94.46) * mm, "end": v(-45, 90.46) * mm});
            skLineSegment(sketch, "E349.trimOffspring", {"start": v(-45, 94.46) * mm, "end": v(-49, 94.46) * mm});
            skLineSegment(sketch, "E350.trimOffspring", {"start": v(-50, 94.46) * mm, "end": v(-54, 94.46) * mm});
            skLineSegment(sketch, "E351.trimOffspring", {"start": v(-50, 94.46) * mm, "end": v(-50, 90.46) * mm});
            skLineSegment(sketch, "E352.trimOffspring", {"start": v(-50, 95.46) * mm, "end": v(-54, 95.46) * mm});
            skLineSegment(sketch, "E353.trimOffspring", {"start": v(-30, 89.46) * mm, "end": v(-34, 89.46) * mm});
            skLineSegment(sketch, "E354.trimOffspring", {"start": v(-30, 90.46) * mm, "end": v(-34, 90.46) * mm});
            skLineSegment(sketch, "E355.trimOffspring", {"start": v(-29, 89.46) * mm, "end": v(-29, 85.46) * mm});
            skLineSegment(sketch, "E356.trimOffspring", {"start": v(-30, 89.46) * mm, "end": v(-30, 85.46) * mm});
            skLineSegment(sketch, "E357.trimOffspring", {"start": v(-34, 94.46) * mm, "end": v(-34, 90.46) * mm});
            skLineSegment(sketch, "E358.trimOffspring", {"start": v(-35, 94.46) * mm, "end": v(-35, 90.46) * mm});
            skLineSegment(sketch, "E359.trimOffspring", {"start": v(-35, 95.46) * mm, "end": v(-39, 95.46) * mm});
            skLineSegment(sketch, "E360.trimOffspring", {"start": v(-35, 94.46) * mm, "end": v(-39, 94.46) * mm});
            skLineSegment(sketch, "E361.trimOffspring", {"start": v(-34, 99.46) * mm, "end": v(-34, 95.46) * mm});
            skLineSegment(sketch, "E362.trimOffspring", {"start": v(-35, 100.46) * mm, "end": v(-39, 100.46) * mm});
            skLineSegment(sketch, "E363.trimOffspring", {"start": v(-35, 99.46) * mm, "end": v(-35, 95.46) * mm});
            skLineSegment(sketch, "E364.trimOffspring", {"start": v(-35, 99.46) * mm, "end": v(-39, 99.46) * mm});
            skLineSegment(sketch, "E365.trimOffspring", {"start": v(-35, 104.46) * mm, "end": v(-35, 100.46) * mm});
            skLineSegment(sketch, "E366.trimOffspring", {"start": v(-35, 105.46) * mm, "end": v(-39, 105.46) * mm});
            skLineSegment(sketch, "E367.trimOffspring", {"start": v(-34, 104.46) * mm, "end": v(-34, 100.46) * mm});
            skLineSegment(sketch, "E368.trimOffspring", {"start": v(-35, 104.46) * mm, "end": v(-39, 104.46) * mm});
            skLineSegment(sketch, "E369.trimOffspring", {"start": v(-35, 109.46) * mm, "end": v(-39, 109.46) * mm});
            skLineSegment(sketch, "E370.trimOffspring", {"start": v(-35, 109.46) * mm, "end": v(-35, 105.46) * mm});
            skLineSegment(sketch, "E371.trimOffspring", {"start": v(-34, 109.46) * mm, "end": v(-34, 105.46) * mm});
            skLineSegment(sketch, "E372.trimOffspring", {"start": v(-35, 110.46) * mm, "end": v(-39, 110.46) * mm});
            skLineSegment(sketch, "E373.trimOffspring", {"start": v(-30, 99.46) * mm, "end": v(-30, 95.46) * mm});
            skLineSegment(sketch, "E374.trimOffspring", {"start": v(-30, 100.46) * mm, "end": v(-34, 100.46) * mm});
            skLineSegment(sketch, "E375.trimOffspring", {"start": v(-29, 99.46) * mm, "end": v(-29, 95.46) * mm});
            skLineSegment(sketch, "E376.trimOffspring", {"start": v(-30, 99.46) * mm, "end": v(-34, 99.46) * mm});
            skLineSegment(sketch, "E377.trimOffspring", {"start": v(-49, 85.46) * mm, "end": v(-45, 85.46) * mm});
            skLineSegment(sketch, "E378", {"start": v(-49, 89.46) * mm, "end": v(-49, 85.46) * mm});
            skLineSegment(sketch, "E379.trimOffspring", {"start": v(-54, 118.96) * mm, "end": v(-50, 118.96) * mm});
            skLineSegment(sketch, "E380.trimOffspring", {"start": v(-50, 115.46) * mm, "end": v(-54, 115.46) * mm});
            skLineSegment(sketch, "E381.trimOffspring", {"start": v(-50, 114.46) * mm, "end": v(-50, 110.46) * mm});
            skLineSegment(sketch, "E382.trimOffspring", {"start": v(-49, 114.46) * mm, "end": v(-49, 110.46) * mm});
            skLineSegment(sketch, "E383.trimOffspring", {"start": v(-50, 114.46) * mm, "end": v(-54, 114.46) * mm});
            skLineSegment(sketch, "E384.trimOffspring", {"start": v(-44, 114.46) * mm, "end": v(-44, 110.46) * mm});
            skLineSegment(sketch, "E385.trimOffspring", {"start": v(-45, 115.46) * mm, "end": v(-49, 115.46) * mm});
            skLineSegment(sketch, "E386.trimOffspring", {"start": v(-44, 118.96) * mm, "end": v(-40, 118.96) * mm});
            skLineSegment(sketch, "E387", {"start": v(-49, 118.96) * mm, "end": v(-45, 118.96) * mm});
            skLineSegment(sketch, "E388", {"start": v(-45, 110.46) * mm, "end": v(-45, 114.46) * mm});
            skLineSegment(sketch, "E389", {"start": v(-45, 114.46) * mm, "end": v(-49, 114.46) * mm});
            skLineSegment(sketch, "E390.trimOffspring", {"start": v(-39, 118.96) * mm, "end": v(-35, 118.96) * mm});
            skLineSegment(sketch, "E391.trimOffspring", {"start": v(-34, 118.96) * mm, "end": v(-30, 118.96) * mm});
            skLineSegment(sketch, "E392.trimOffspring", {"start": v(-35, 114.46) * mm, "end": v(-44, 114.46) * mm});
            skLineSegment(sketch, "E393.trimOffspring", {"start": v(-34, 114.46) * mm, "end": v(-34, 110.46) * mm});
            skLineSegment(sketch, "E394.trimOffspring", {"start": v(-35, 115.46) * mm, "end": v(-44, 115.46) * mm});
            skLineSegment(sketch, "E395.trimOffspring", {"start": v(-35, 114.46) * mm, "end": v(-35, 110.46) * mm});
            skLineSegment(sketch, "E396.trimOffspring", {"start": v(-39, 114.46) * mm, "end": v(-39, 110.46) * mm});
            skLineSegment(sketch, "E397.trimOffspring", {"start": v(-40, 114.46) * mm, "end": v(-40, 110.46) * mm});
            skLineSegment(sketch, "E398.trimOffspring", {"start": v(-30, 109.46) * mm, "end": v(-34, 109.46) * mm});
            skLineSegment(sketch, "E399.trimOffspring", {"start": v(-30, 109.46) * mm, "end": v(-30, 105.46) * mm});
            skLineSegment(sketch, "E400.trimOffspring", {"start": v(-30, 110.46) * mm, "end": v(-34, 110.46) * mm});
            skLineSegment(sketch, "E401.trimOffspring", {"start": v(-29, 109.46) * mm, "end": v(-29, 105.46) * mm});
            skLineSegment(sketch, "E402.trimOffspring", {"start": v(-30, 114.46) * mm, "end": v(-34, 114.46) * mm});
            skLineSegment(sketch, "E403.trimOffspring", {"start": v(-30, 114.46) * mm, "end": v(-30, 110.46) * mm});
            skLineSegment(sketch, "E404.trimOffspring", {"start": v(-30, 115.46) * mm, "end": v(-34, 115.46) * mm});
            skLineSegment(sketch, "E405.trimOffspring", {"start": v(-29, 114.46) * mm, "end": v(-29, 110.46) * mm});
            skLineSegment(sketch, "E406.trimOffspring", {"start": v(-25, 114.46) * mm, "end": v(-25, 110.46) * mm});
            skLineSegment(sketch, "E407.trimOffspring", {"start": v(-25, 115.46) * mm, "end": v(-29, 115.46) * mm});
            skLineSegment(sketch, "E408.trimOffspring", {"start": v(-24, 114.46) * mm, "end": v(-24, 110.46) * mm});
            skLineSegment(sketch, "E409.trimOffspring", {"start": v(-25, 114.46) * mm, "end": v(-29, 114.46) * mm});
            skLineSegment(sketch, "E410.trimOffspring", {"start": v(-25, 110.46) * mm, "end": v(-29, 110.46) * mm});
            skLineSegment(sketch, "E411.trimOffspring", {"start": v(-25, 109.46) * mm, "end": v(-29, 109.46) * mm});
            skLineSegment(sketch, "E412.trimOffspring", {"start": v(-20, 109.46) * mm, "end": v(-24, 109.46) * mm});
            skLineSegment(sketch, "E413.trimOffspring", {"start": v(-20, 109.46) * mm, "end": v(-20, 105.46) * mm});
            skLineSegment(sketch, "E414.trimOffspring", {"start": v(-19, 109.46) * mm, "end": v(-19, 105.46) * mm});
            skLineSegment(sketch, "E415.trimOffspring", {"start": v(-20, 110.46) * mm, "end": v(-24, 110.46) * mm});
            skLineSegment(sketch, "E416.trimOffspring", {"start": v(-15, 109.46) * mm, "end": v(-15, 105.46) * mm});
            skLineSegment(sketch, "E417.trimOffspring", {"start": v(-15, 110.46) * mm, "end": v(-19, 110.46) * mm});
            skLineSegment(sketch, "E418.trimOffspring", {"start": v(-14, 109.46) * mm, "end": v(-14, 105.46) * mm});
            skLineSegment(sketch, "E419.trimOffspring", {"start": v(-15, 109.46) * mm, "end": v(-19, 109.46) * mm});
            skLineSegment(sketch, "E420.trimOffspring", {"start": v(-15, 114.46) * mm, "end": v(-19, 114.46) * mm});
            skLineSegment(sketch, "E421.trimOffspring", {"start": v(-15, 114.46) * mm, "end": v(-15, 110.46) * mm});
            skLineSegment(sketch, "E422.trimOffspring", {"start": v(-15, 115.46) * mm, "end": v(-19, 115.46) * mm});
            skLineSegment(sketch, "E423.trimOffspring", {"start": v(-14, 114.46) * mm, "end": v(-14, 110.46) * mm});
            skLineSegment(sketch, "E424.trimOffspring", {"start": v(-14, 118.96) * mm, "end": v(-10, 118.96) * mm});
            skLineSegment(sketch, "E425.trimOffspring", {"start": v(-19, 118.96) * mm, "end": v(-15, 118.96) * mm});
            skLineSegment(sketch, "E426", {"start": v(-29, 118.96) * mm, "end": v(-25, 118.96) * mm});
            skLineSegment(sketch, "E427", {"start": v(-25, 118.96) * mm, "end": v(-25, 115.46) * mm});
            skLineSegment(sketch, "E428", {"start": v(-24, 115.46) * mm, "end": v(-24, 118.96) * mm});
            skLineSegment(sketch, "E429", {"start": v(-24, 118.96) * mm, "end": v(-20, 118.96) * mm});
            skLineSegment(sketch, "E430.trimOffspring", {"start": v(-20, 114.46) * mm, "end": v(-20, 110.46) * mm});
            skLineSegment(sketch, "E431.trimOffspring", {"start": v(-20, 115.46) * mm, "end": v(-24, 115.46) * mm});
            skLineSegment(sketch, "E432.trimOffspring", {"start": v(-20, 114.46) * mm, "end": v(-24, 114.46) * mm});
            skLineSegment(sketch, "E433", {"start": v(-20, 118.96) * mm, "end": v(-20, 115.46) * mm});
            skLineSegment(sketch, "E434", {"start": v(-19, 114.46) * mm, "end": v(-19, 110.46) * mm});
            skLineSegment(sketch, "E435.trimOffspring", {"start": v(-9, 109.46) * mm, "end": v(-9, 105.46) * mm});
            skLineSegment(sketch, "E436.trimOffspring", {"start": v(-10, 110.46) * mm, "end": v(-14, 110.46) * mm});
            skLineSegment(sketch, "E437.trimOffspring", {"start": v(-10, 109.46) * mm, "end": v(-10, 105.46) * mm});
            skLineSegment(sketch, "E438.trimOffspring", {"start": v(-10, 109.46) * mm, "end": v(-14, 109.46) * mm});
            skLineSegment(sketch, "E439.trimOffspring", {"start": v(-10, 114.46) * mm, "end": v(-10, 110.46) * mm});
            skLineSegment(sketch, "E440.trimOffspring", {"start": v(-10, 115.46) * mm, "end": v(-14, 115.46) * mm});
            skLineSegment(sketch, "E441.trimOffspring", {"start": v(-9, 114.46) * mm, "end": v(-9, 110.46) * mm});
            skLineSegment(sketch, "E442.trimOffspring", {"start": v(-10, 114.46) * mm, "end": v(-14, 114.46) * mm});
            skLineSegment(sketch, "E443.trimOffspring", {"start": v(-9, 118.96) * mm, "end": v(-5, 118.96) * mm});
            skLineSegment(sketch, "E444", {"start": v(-10, 118.96) * mm, "end": v(-10, 115.46) * mm});
            skLineSegment(sketch, "E445.trimOffspring", {"start": v(-30, 104.46) * mm, "end": v(-30, 100.46) * mm});
            skLineSegment(sketch, "E446.trimOffspring", {"start": v(-30, 105.46) * mm, "end": v(-34, 105.46) * mm});
            skLineSegment(sketch, "E447.trimOffspring", {"start": v(-29, 104.46) * mm, "end": v(-29, 100.46) * mm});
            skLineSegment(sketch, "E448.trimOffspring", {"start": v(-30, 104.46) * mm, "end": v(-34, 104.46) * mm});
            skLineSegment(sketch, "E449.trimOffspring", {"start": v(-29, 94.46) * mm, "end": v(-29, 90.46) * mm});
            skLineSegment(sketch, "E450.trimOffspring", {"start": v(-30, 95.46) * mm, "end": v(-34, 95.46) * mm});
            skLineSegment(sketch, "E451.trimOffspring", {"start": v(-30, 94.46) * mm, "end": v(-30, 90.46) * mm});
            skLineSegment(sketch, "E452.trimOffspring", {"start": v(-30, 94.46) * mm, "end": v(-34, 94.46) * mm});
            skLineSegment(sketch, "E453.trimOffspring", {"start": v(-20, 104.46) * mm, "end": v(-20, 100.46) * mm});
            skLineSegment(sketch, "E454.trimOffspring", {"start": v(-20, 105.46) * mm, "end": v(-24, 105.46) * mm});
            skLineSegment(sketch, "E455.trimOffspring", {"start": v(-19, 104.46) * mm, "end": v(-19, 100.46) * mm});
            skLineSegment(sketch, "E456.trimOffspring", {"start": v(-20, 104.46) * mm, "end": v(-24, 104.46) * mm});
            skLineSegment(sketch, "E457.trimOffspring", {"start": v(-24, 104.46) * mm, "end": v(-24, 100.46) * mm});
            skLineSegment(sketch, "E458.trimOffspring", {"start": v(-25, 105.46) * mm, "end": v(-29, 105.46) * mm});
            skLineSegment(sketch, "E459.trimOffspring", {"start": v(-25, 104.46) * mm, "end": v(-25, 100.46) * mm});
            skLineSegment(sketch, "E460.trimOffspring", {"start": v(-25, 104.46) * mm, "end": v(-29, 104.46) * mm});
            skLineSegment(sketch, "E461.trimOffspring", {"start": v(-14, 104.46) * mm, "end": v(-14, 100.46) * mm});
            skLineSegment(sketch, "E462.trimOffspring", {"start": v(-15, 105.46) * mm, "end": v(-19, 105.46) * mm});
            skLineSegment(sketch, "E463.trimOffspring", {"start": v(-15, 104.46) * mm, "end": v(-15, 100.46) * mm});
            skLineSegment(sketch, "E464.trimOffspring", {"start": v(-15, 104.46) * mm, "end": v(-19, 104.46) * mm});
            skLineSegment(sketch, "E465.trimOffspring", {"start": v(-14, 99.46) * mm, "end": v(-14, 95.46) * mm});
            skLineSegment(sketch, "E466.trimOffspring", {"start": v(-15, 100.46) * mm, "end": v(-19, 100.46) * mm});
            skLineSegment(sketch, "E467.trimOffspring", {"start": v(-15, 99.46) * mm, "end": v(-15, 95.46) * mm});
            skLineSegment(sketch, "E468.trimOffspring", {"start": v(-19, 99.46) * mm, "end": v(-19, 95.46) * mm});
            skLineSegment(sketch, "E469.trimOffspring", {"start": v(-20, 100.46) * mm, "end": v(-24, 100.46) * mm});
            skLineSegment(sketch, "E470.trimOffspring", {"start": v(-20, 99.46) * mm, "end": v(-20, 95.46) * mm});
            skLineSegment(sketch, "E471.trimOffspring", {"start": v(-20, 99.46) * mm, "end": v(-24, 99.46) * mm});
            skLineSegment(sketch, "E472.trimOffspring", {"start": v(-24, 99.46) * mm, "end": v(-24, 95.46) * mm});
            skLineSegment(sketch, "E473.trimOffspring", {"start": v(-25, 100.46) * mm, "end": v(-29, 100.46) * mm});
            skLineSegment(sketch, "E474.trimOffspring", {"start": v(-25, 99.46) * mm, "end": v(-25, 95.46) * mm});
            skLineSegment(sketch, "E475.trimOffspring", {"start": v(-25, 99.46) * mm, "end": v(-29, 99.46) * mm});
            skLineSegment(sketch, "E476.trimOffspring", {"start": v(-25, 94.46) * mm, "end": v(-25, 90.46) * mm});
            skLineSegment(sketch, "E477.trimOffspring", {"start": v(-24, 94.46) * mm, "end": v(-24, 90.46) * mm});
            skLineSegment(sketch, "E478.trimOffspring", {"start": v(-25, 95.46) * mm, "end": v(-29, 95.46) * mm});
            skLineSegment(sketch, "E479.trimOffspring", {"start": v(-25, 94.46) * mm, "end": v(-29, 94.46) * mm});
            skLineSegment(sketch, "E480.trimOffspring", {"start": v(-25, 90.46) * mm, "end": v(-29, 90.46) * mm});
            skLineSegment(sketch, "E481.trimOffspring", {"start": v(-25, 89.46) * mm, "end": v(-25, 85.46) * mm});
            skLineSegment(sketch, "E482.trimOffspring", {"start": v(-24, 89.46) * mm, "end": v(-24, 85.46) * mm});
            skLineSegment(sketch, "E483.trimOffspring", {"start": v(-25, 89.46) * mm, "end": v(-29, 89.46) * mm});
            skLineSegment(sketch, "E484", {"start": v(-19, 99.46) * mm, "end": v(-15, 99.46) * mm});
            skLineSegment(sketch, "E485.trimOffspring", {"start": v(-10, 104.46) * mm, "end": v(-10, 100.46) * mm});
            skLineSegment(sketch, "E486.trimOffspring", {"start": v(-10, 105.46) * mm, "end": v(-14, 105.46) * mm});
            skLineSegment(sketch, "E487.trimOffspring", {"start": v(-9, 104.46) * mm, "end": v(-9, 100.46) * mm});
            skLineSegment(sketch, "E488.trimOffspring", {"start": v(-10, 104.46) * mm, "end": v(-14, 104.46) * mm});
            skLineSegment(sketch, "E489.trimOffspring", {"start": v(-10, 100.46) * mm, "end": v(-14, 100.46) * mm});
            skLineSegment(sketch, "E490.trimOffspring", {"start": v(-10, 99.46) * mm, "end": v(-10, 95.46) * mm});
            skLineSegment(sketch, "E491.trimOffspring", {"start": v(-10, 99.46) * mm, "end": v(-14, 99.46) * mm});
            skLineSegment(sketch, "E492.trimOffspring", {"start": v(-9, 99.46) * mm, "end": v(-9, 95.46) * mm});
            skLineSegment(sketch, "E493.trimOffspring", {"start": v(-10, 89.46) * mm, "end": v(-14, 89.46) * mm});
            skLineSegment(sketch, "E494.trimOffspring", {"start": v(-10, 90.46) * mm, "end": v(-14, 90.46) * mm});
            skLineSegment(sketch, "E495.trimOffspring", {"start": v(-9, 89.46) * mm, "end": v(-9, 85.46) * mm});
            skLineSegment(sketch, "E496.trimOffspring", {"start": v(-10, 89.46) * mm, "end": v(-10, 85.46) * mm});
            skLineSegment(sketch, "E497.trimOffspring", {"start": v(-9, 94.46) * mm, "end": v(-9, 90.46) * mm});
            skLineSegment(sketch, "E498.trimOffspring", {"start": v(-10, 95.46) * mm, "end": v(-14, 95.46) * mm});
            skLineSegment(sketch, "E499.trimOffspring", {"start": v(-10, 94.46) * mm, "end": v(-10, 90.46) * mm});
            skLineSegment(sketch, "E500.trimOffspring", {"start": v(-10, 94.46) * mm, "end": v(-14, 94.46) * mm});
            skLineSegment(sketch, "E501.trimOffspring", {"start": v(-14, 94.46) * mm, "end": v(-14, 90.46) * mm});
            skLineSegment(sketch, "E502.trimOffspring", {"start": v(-15, 95.46) * mm, "end": v(-19, 95.46) * mm});
            skLineSegment(sketch, "E503.trimOffspring", {"start": v(-15, 94.46) * mm, "end": v(-15, 90.46) * mm});
            skLineSegment(sketch, "E504.trimOffspring", {"start": v(-15, 94.46) * mm, "end": v(-19, 94.46) * mm});
            skLineSegment(sketch, "E505.trimOffspring", {"start": v(-14, 89.46) * mm, "end": v(-14, 85.46) * mm});
            skLineSegment(sketch, "E506.trimOffspring", {"start": v(-15, 90.46) * mm, "end": v(-19, 90.46) * mm});
            skLineSegment(sketch, "E507.trimOffspring", {"start": v(-15, 89.46) * mm, "end": v(-15, 85.46) * mm});
            skLineSegment(sketch, "E508.trimOffspring", {"start": v(-15, 89.46) * mm, "end": v(-19, 89.46) * mm});
            skLineSegment(sketch, "E509.trimOffspring", {"start": v(-19, 89.46) * mm, "end": v(-19, 85.46) * mm});
            skLineSegment(sketch, "E510.trimOffspring", {"start": v(-20, 90.46) * mm, "end": v(-24, 90.46) * mm});
            skLineSegment(sketch, "E511.trimOffspring", {"start": v(-20, 89.46) * mm, "end": v(-20, 85.46) * mm});
            skLineSegment(sketch, "E512.trimOffspring", {"start": v(-20, 89.46) * mm, "end": v(-24, 89.46) * mm});
            skLineSegment(sketch, "E513.trimOffspring", {"start": v(-24, 85.46) * mm, "end": v(-20, 85.46) * mm});
            skLineSegment(sketch, "E514.trimOffspring", {"start": v(-19, 85.46) * mm, "end": v(-15, 85.46) * mm});
            skLineSegment(sketch, "E515.trimOffspring", {"start": v(-14, 85.46) * mm, "end": v(-10, 85.46) * mm});
            skLineSegment(sketch, "E516.trimOffspring", {"start": v(-5, 89.46) * mm, "end": v(-5, 85.46) * mm});
            skLineSegment(sketch, "E517.trimOffspring", {"start": v(-9, 85.46) * mm, "end": v(-5, 85.46) * mm});
            skLineSegment(sketch, "E518.trimOffspring", {"start": v(-5, 99.46) * mm, "end": v(-5, 95.46) * mm});
            skLineSegment(sketch, "E519", {"start": v(-9, 94.46) * mm, "end": v(-5, 94.46) * mm});
            skLineSegment(sketch, "E520", {"start": v(-5, 94.46) * mm, "end": v(-5, 90.46) * mm});
            skLineSegment(sketch, "E521.trimOffspring", {"start": v(-5, 104.46) * mm, "end": v(-5, 100.46) * mm});
            skLineSegment(sketch, "E522.trimOffspring", {"start": v(-5, 109.46) * mm, "end": v(-5, 105.46) * mm});
            skLineSegment(sketch, "E523.trimOffspring", {"start": v(-5, 114.46) * mm, "end": v(-5, 110.46) * mm});
            skLineSegment(sketch, "E524.trimOffspring", {"start": v(-94, 104.46) * mm, "end": v(-94, 100.46) * mm});
            skLineSegment(sketch, "E525.trimOffspring", {"start": v(-4.5, 90.46) * mm, "end": v(-4.5, 89.46) * mm});
            skLineSegment(sketch, "E526.trimOffspring", {"start": v(-4.5, 95.46) * mm, "end": v(-4.5, 94.46) * mm});
            skLineSegment(sketch, "E527.trimOffspring", {"start": v(-4.5, 100.46) * mm, "end": v(-4.5, 99.46) * mm});
            skPoint(sketch, "E528", {"position": v(-50, 118.96) * mm});
            skLineSegment(sketch, "E529.trimOffspring", {"start": v(-24, 109.46) * mm, "end": v(-24, 105.46) * mm});
            skLineSegment(sketch, "E530.trimOffspring", {"start": v(-25, 109.46) * mm, "end": v(-25, 105.46) * mm});
            skLineSegment(sketch, "E531.trimOffspring", {"start": v(-19, 94.46) * mm, "end": v(-19, 90.46) * mm});
            skLineSegment(sketch, "E532.trimOffspring", {"start": v(-20, 95.46) * mm, "end": v(-24, 95.46) * mm});
            skLineSegment(sketch, "E533.trimOffspring", {"start": v(-20, 94.46) * mm, "end": v(-20, 90.46) * mm});
            skLineSegment(sketch, "E534.trimOffspring", {"start": v(-20, 94.46) * mm, "end": v(-24, 94.46) * mm});
            skLineSegment(sketch, "E535", {"start": v(0, 82.46) * mm, "end": v(-5, 82.46) * mm});
            skLineSegment(sketch, "E536", {"start": v(-5, 82.46) * mm, "end": v(-5, 85.46) * mm});
            skLineSegment(sketch, "E537.trimOffspring", {"start": v(-84, 85.46) * mm, "end": v(-80, 85.46) * mm});
            skSolve(sketch);
        }
        {
            var Q0;
            Q0=qSketchRegion(id+"F10",true);
            extrude(context, id + "F11", {"entities" : qUnion([Q0]), "operationType" : NewBodyOperationType.REMOVE, "oppositeDirection" : true, "depth" : 5 * mm, "offsetDistance" : 25 * mm});
        }
        {
            var Q0;
            Q0=makeQuery(id+"F7.boolean.opBoolean","MERGE",FACE,{"derivedFrom":[makeQuery(id+"F1.opExtrude","SWEPT_FACE",FACE,{"disambiguationData":[OSD([sQuery(id+"F0.wireOp",EDGE,"E3")])]}),makeQuery(id+"F7.opExtrude","CAP_FACE",FACE,{"disambiguationData":[OSD([sQuery(id+"F6.wireOp",EDGE,"E15.bottom"),sQuery(id+"F6.wireOp",EDGE,"E15.top"),sQuery(id+"F6.wireOp",EDGE,"E15.left"),sQuery(id+"F6.wireOp",EDGE,"E15.right")])],"isStart":true})]});
            var sketch = newSketch(context, id + "F12", { "sketchPlane" : qUnion([Q0])});
            skLineSegment(sketch, "E538", {"start": v(-50.5, 33) * mm, "end": v(-50.5, 32.5) * mm});
            skLineSegment(sketch, "E539", {"start": v(-50.5, 22.5) * mm, "end": v(-50.5, 22) * mm});
            skLineSegment(sketch, "E540", {"start": v(-50.5, 17.5) * mm, "end": v(-50.5, 17) * mm});
            skLineSegment(sketch, "E541", {"start": v(-50.5, 12.5) * mm, "end": v(-50.5, 12) * mm});
            skLineSegment(sketch, "E542.0", {"start": v(-140, 3) * mm, "end": v(-136, 3) * mm});
            skLineSegment(sketch, "E543.0", {"start": v(-51, 8) * mm, "end": v(-55, 8) * mm});
            skLineSegment(sketch, "E544.0", {"start": v(-51, 7) * mm, "end": v(-55, 7) * mm});
            skLineSegment(sketch, "E545.0", {"start": v(-51, 13) * mm, "end": v(-55, 13) * mm});
            skLineSegment(sketch, "E546.0", {"start": v(-51, 18) * mm, "end": v(-55, 18) * mm});
            skLineSegment(sketch, "E547.0", {"start": v(-51, 17) * mm, "end": v(-55, 17) * mm});
            skLineSegment(sketch, "E548.0", {"start": v(-51, 23) * mm, "end": v(-55, 23) * mm});
            skLineSegment(sketch, "E549.0", {"start": v(-51, 22) * mm, "end": v(-55, 22) * mm});
            skLineSegment(sketch, "E550.0", {"start": v(-51, 28) * mm, "end": v(-55, 28) * mm});
            skLineSegment(sketch, "E551.0", {"start": v(-51, 27) * mm, "end": v(-55, 27) * mm});
            skLineSegment(sketch, "E552.0", {"start": v(-51, 33) * mm, "end": v(-55, 33) * mm});
            skLineSegment(sketch, "E553.0", {"start": v(-51, 32) * mm, "end": v(-55, 32) * mm});
            skLineSegment(sketch, "E554.0", {"start": v(-130, 36.5) * mm, "end": v(-130, 33) * mm});
            skLineSegment(sketch, "E555.0", {"start": v(-126, 36.5) * mm, "end": v(-126, 33) * mm});
            skLineSegment(sketch, "E556.0", {"start": v(-121, 36.5) * mm, "end": v(-121, 33) * mm});
            skLineSegment(sketch, "E557.0", {"start": v(-120, 36.5) * mm, "end": v(-120, 33) * mm});
            skLineSegment(sketch, "E558.0", {"start": v(-116, 36.5) * mm, "end": v(-116, 33) * mm});
            skLineSegment(sketch, "E559.0", {"start": v(-115, 36.5) * mm, "end": v(-115, 33) * mm});
            skLineSegment(sketch, "E560.0", {"start": v(-111, 36.5) * mm, "end": v(-111, 33) * mm});
            skLineSegment(sketch, "E561.0", {"start": v(-110, 36.5) * mm, "end": v(-110, 33) * mm});
            skLineSegment(sketch, "E562.0", {"start": v(-106, 36.5) * mm, "end": v(-106, 33) * mm});
            skLineSegment(sketch, "E563.0", {"start": v(-105, 36.5) * mm, "end": v(-105, 33) * mm});
            skLineSegment(sketch, "E564.0", {"start": v(-101, 36.5) * mm, "end": v(-101, 33) * mm});
            skLineSegment(sketch, "E565.0", {"start": v(-100, 36.5) * mm, "end": v(-100, 33) * mm});
            skLineSegment(sketch, "E566.0", {"start": v(-96, 36.5) * mm, "end": v(-96, 33) * mm});
            skLineSegment(sketch, "E567.0", {"start": v(-95, 36.5) * mm, "end": v(-95, 33) * mm});
            skLineSegment(sketch, "E568.0", {"start": v(-91, 36.5) * mm, "end": v(-91, 33) * mm});
            skLineSegment(sketch, "E569.0", {"start": v(-90, 36.5) * mm, "end": v(-90, 33) * mm});
            skLineSegment(sketch, "E570.0", {"start": v(-86, 36.5) * mm, "end": v(-86, 33) * mm});
            skLineSegment(sketch, "E571.0", {"start": v(-85, 36.5) * mm, "end": v(-85, 33) * mm});
            skLineSegment(sketch, "E572.0", {"start": v(-81, 36.5) * mm, "end": v(-81, 33) * mm});
            skLineSegment(sketch, "E573.0", {"start": v(-80, 36.5) * mm, "end": v(-80, 33) * mm});
            skLineSegment(sketch, "E574.0", {"start": v(-76, 36.5) * mm, "end": v(-76, 33) * mm});
            skLineSegment(sketch, "E575.0", {"start": v(-75, 36.5) * mm, "end": v(-75, 33) * mm});
            skLineSegment(sketch, "E576.0", {"start": v(-65, 36.5) * mm, "end": v(-65, 33) * mm});
            skLineSegment(sketch, "E577.0", {"start": v(-61, 36.5) * mm, "end": v(-61, 33) * mm});
            skLineSegment(sketch, "E578.0", {"start": v(-60, 36.5) * mm, "end": v(-60, 33) * mm});
            skLineSegment(sketch, "E579.0", {"start": v(-55, 36.5) * mm, "end": v(-55, 33) * mm});
            skLineSegment(sketch, "E580.trimOffspring", {"start": v(-50.5, 23) * mm, "end": v(-50.5, 22.5) * mm});
            skLineSegment(sketch, "E581.trimOffspring", {"start": v(-50.5, 18) * mm, "end": v(-50.5, 17.5) * mm});
            skLineSegment(sketch, "E582.trimOffspring", {"start": v(-50.5, 13) * mm, "end": v(-50.5, 12.5) * mm});
            skLineSegment(sketch, "E583.0", {"start": v(-51, 36.5) * mm, "end": v(-51, 33) * mm});
            skPoint(sketch, "E584.trimOffspring.end.orphan", {"position": v(-141.54, 35.15) * mm});
            skLineSegment(sketch, "E585.trimOffspring", {"start": v(-130, 36.5) * mm, "end": v(-126, 36.5) * mm});
            skLineSegment(sketch, "E586.trimOffspring", {"start": v(-125, 36.5) * mm, "end": v(-121, 36.5) * mm});
            skLineSegment(sketch, "E587.trimOffspring", {"start": v(-121, 33) * mm, "end": v(-125, 33) * mm});
            skLineSegment(sketch, "E588.trimOffspring", {"start": v(-120, 32) * mm, "end": v(-120, 28) * mm});
            skLineSegment(sketch, "E589.trimOffspring", {"start": v(-121, 32) * mm, "end": v(-121, 28) * mm});
            skLineSegment(sketch, "E590.trimOffspring", {"start": v(-121, 32) * mm, "end": v(-125, 32) * mm});
            skLineSegment(sketch, "E591.trimOffspring", {"start": v(-125, 32) * mm, "end": v(-125, 28) * mm});
            skLineSegment(sketch, "E592.trimOffspring", {"start": v(-126, 32) * mm, "end": v(-126, 28) * mm});
            skLineSegment(sketch, "E593.trimOffspring", {"start": v(-126, 32) * mm, "end": v(-130, 32) * mm});
            skLineSegment(sketch, "E594.trimOffspring", {"start": v(-120, 36.5) * mm, "end": v(-116, 36.5) * mm});
            skLineSegment(sketch, "E595.trimOffspring", {"start": v(-115, 36.5) * mm, "end": v(-111, 36.5) * mm});
            skLineSegment(sketch, "E596.trimOffspring", {"start": v(-131, 32) * mm, "end": v(-131, 28) * mm});
            skLineSegment(sketch, "E597.trimOffspring", {"start": v(-131, 32) * mm, "end": v(-135, 32) * mm});
            skLineSegment(sketch, "E598.trimOffspring", {"start": v(-131, 28) * mm, "end": v(-135, 28) * mm});
            skLineSegment(sketch, "E599.trimOffspring", {"start": v(-130, 27) * mm, "end": v(-130, 23) * mm});
            skLineSegment(sketch, "E600.trimOffspring", {"start": v(-131, 27) * mm, "end": v(-131, 23) * mm});
            skLineSegment(sketch, "E601.trimOffspring", {"start": v(-131, 27) * mm, "end": v(-135, 27) * mm});
            skLineSegment(sketch, "E602.trimOffspring", {"start": v(-136, 27) * mm, "end": v(-136, 23) * mm});
            skLineSegment(sketch, "E603.trimOffspring", {"start": v(-135, 27) * mm, "end": v(-135, 23) * mm});
            skLineSegment(sketch, "E604.trimOffspring", {"start": v(-136, 28) * mm, "end": v(-140, 28) * mm});
            skLineSegment(sketch, "E605.trimOffspring", {"start": v(-136, 27) * mm, "end": v(-140, 27) * mm});
            skLineSegment(sketch, "E606.trimOffspring", {"start": v(-135, 32) * mm, "end": v(-135, 28) * mm});
            skLineSegment(sketch, "E607.trimOffspring", {"start": v(-136, 32) * mm, "end": v(-136, 28) * mm});
            skLineSegment(sketch, "E608.trimOffspring", {"start": v(-126, 27) * mm, "end": v(-126, 23) * mm});
            skLineSegment(sketch, "E609.trimOffspring", {"start": v(-126, 28) * mm, "end": v(-130, 28) * mm});
            skLineSegment(sketch, "E610.trimOffspring", {"start": v(-125, 27) * mm, "end": v(-125, 23) * mm});
            skLineSegment(sketch, "E611.trimOffspring", {"start": v(-126, 27) * mm, "end": v(-130, 27) * mm});
            skLineSegment(sketch, "E612.trimOffspring", {"start": v(-121, 27) * mm, "end": v(-125, 27) * mm});
            skLineSegment(sketch, "E613.trimOffspring", {"start": v(-120, 27) * mm, "end": v(-120, 23) * mm});
            skLineSegment(sketch, "E614.trimOffspring", {"start": v(-121, 27) * mm, "end": v(-121, 23) * mm});
            skLineSegment(sketch, "E615.trimOffspring", {"start": v(-121, 28) * mm, "end": v(-125, 28) * mm});
            skLineSegment(sketch, "E616.trimOffspring", {"start": v(-116, 27) * mm, "end": v(-116, 23) * mm});
            skLineSegment(sketch, "E617.trimOffspring", {"start": v(-116, 28) * mm, "end": v(-120, 28) * mm});
            skLineSegment(sketch, "E618.trimOffspring", {"start": v(-115, 27) * mm, "end": v(-115, 23) * mm});
            skLineSegment(sketch, "E619.trimOffspring", {"start": v(-116, 27) * mm, "end": v(-120, 27) * mm});
            skLineSegment(sketch, "E620.trimOffspring", {"start": v(-116, 32) * mm, "end": v(-120, 32) * mm});
            skLineSegment(sketch, "E621.trimOffspring", {"start": v(-116, 32) * mm, "end": v(-116, 28) * mm});
            skLineSegment(sketch, "E622.trimOffspring", {"start": v(-116, 33) * mm, "end": v(-120, 33) * mm});
            skLineSegment(sketch, "E623.trimOffspring", {"start": v(-115, 32) * mm, "end": v(-115, 28) * mm});
            skLineSegment(sketch, "E624.trimOffspring", {"start": v(-111, 32) * mm, "end": v(-111, 28) * mm});
            skLineSegment(sketch, "E625.trimOffspring", {"start": v(-111, 33) * mm, "end": v(-115, 33) * mm});
            skLineSegment(sketch, "E626.trimOffspring", {"start": v(-110, 36.5) * mm, "end": v(-106, 36.5) * mm});
            skLineSegment(sketch, "E627.trimOffspring", {"start": v(-111, 32) * mm, "end": v(-115, 32) * mm});
            skLineSegment(sketch, "E628.trimOffspring", {"start": v(-110, 32) * mm, "end": v(-110, 28) * mm});
            skLineSegment(sketch, "E629.trimOffspring", {"start": v(-105, 36.5) * mm, "end": v(-101, 36.5) * mm});
            skLineSegment(sketch, "E630.trimOffspring", {"start": v(-106, 33) * mm, "end": v(-110, 33) * mm});
            skLineSegment(sketch, "E631.trimOffspring", {"start": v(-106, 32) * mm, "end": v(-106, 28) * mm});
            skLineSegment(sketch, "E632.trimOffspring", {"start": v(-106, 32) * mm, "end": v(-110, 32) * mm});
            skLineSegment(sketch, "E633.trimOffspring", {"start": v(-105, 32) * mm, "end": v(-105, 28) * mm});
            skLineSegment(sketch, "E634.trimOffspring", {"start": v(-106, 28) * mm, "end": v(-110, 28) * mm});
            skLineSegment(sketch, "E635.trimOffspring", {"start": v(-106, 27) * mm, "end": v(-106, 23) * mm});
            skLineSegment(sketch, "E636.trimOffspring", {"start": v(-106, 27) * mm, "end": v(-110, 27) * mm});
            skLineSegment(sketch, "E637.trimOffspring", {"start": v(-105, 27) * mm, "end": v(-105, 23) * mm});
            skLineSegment(sketch, "E638.trimOffspring", {"start": v(-110, 27) * mm, "end": v(-110, 23) * mm});
            skLineSegment(sketch, "E639.trimOffspring", {"start": v(-111, 28) * mm, "end": v(-115, 28) * mm});
            skLineSegment(sketch, "E640.trimOffspring", {"start": v(-111, 27) * mm, "end": v(-111, 23) * mm});
            skLineSegment(sketch, "E641.trimOffspring", {"start": v(-111, 27) * mm, "end": v(-115, 27) * mm});
            skLineSegment(sketch, "E642.trimOffspring", {"start": v(-140, 27) * mm, "end": v(-140, 23) * mm});
            skLineSegment(sketch, "E643.trimOffspring", {"start": v(-140, 17) * mm, "end": v(-140, 13) * mm});
            skLineSegment(sketch, "E644.trimOffspring", {"start": v(-136, 17) * mm, "end": v(-136, 13) * mm});
            skLineSegment(sketch, "E645.trimOffspring", {"start": v(-136, 18) * mm, "end": v(-140, 18) * mm});
            skLineSegment(sketch, "E646.trimOffspring", {"start": v(-135, 17) * mm, "end": v(-135, 13) * mm});
            skLineSegment(sketch, "E647.trimOffspring", {"start": v(-136, 17) * mm, "end": v(-140, 17) * mm});
            skLineSegment(sketch, "E648.trimOffspring", {"start": v(-136, 22) * mm, "end": v(-140, 22) * mm});
            skLineSegment(sketch, "E649.trimOffspring", {"start": v(-136, 22) * mm, "end": v(-136, 18) * mm});
            skLineSegment(sketch, "E650.trimOffspring", {"start": v(-136, 23) * mm, "end": v(-140, 23) * mm});
            skLineSegment(sketch, "E651.trimOffspring", {"start": v(-135, 22) * mm, "end": v(-135, 18) * mm});
            skLineSegment(sketch, "E652.trimOffspring", {"start": v(-130, 22) * mm, "end": v(-130, 18) * mm});
            skLineSegment(sketch, "E653.trimOffspring", {"start": v(-131, 23) * mm, "end": v(-135, 23) * mm});
            skLineSegment(sketch, "E654.trimOffspring", {"start": v(-131, 22) * mm, "end": v(-131, 18) * mm});
            skLineSegment(sketch, "E655.trimOffspring", {"start": v(-131, 22) * mm, "end": v(-135, 22) * mm});
            skLineSegment(sketch, "E656.trimOffspring", {"start": v(-126, 22) * mm, "end": v(-126, 18) * mm});
            skLineSegment(sketch, "E657.trimOffspring", {"start": v(-126, 23) * mm, "end": v(-130, 23) * mm});
            skLineSegment(sketch, "E658.trimOffspring", {"start": v(-125, 22) * mm, "end": v(-125, 18) * mm});
            skLineSegment(sketch, "E659.trimOffspring", {"start": v(-126, 22) * mm, "end": v(-130, 22) * mm});
            skLineSegment(sketch, "E660", {"start": v(-125, 36.5) * mm, "end": v(-125, 33) * mm});
            skLineSegment(sketch, "E661.trimOffspring", {"start": v(-126, 33) * mm, "end": v(-130, 33) * mm});
            skLineSegment(sketch, "E662.trimOffspring", {"start": v(-116, 23) * mm, "end": v(-120, 23) * mm});
            skLineSegment(sketch, "E663.trimOffspring", {"start": v(-116, 22) * mm, "end": v(-120, 22) * mm});
            skLineSegment(sketch, "E664.trimOffspring", {"start": v(-115, 22) * mm, "end": v(-115, 18) * mm});
            skLineSegment(sketch, "E665.trimOffspring", {"start": v(-116, 22) * mm, "end": v(-116, 18) * mm});
            skLineSegment(sketch, "E666.trimOffspring", {"start": v(-120, 22) * mm, "end": v(-120, 18) * mm});
            skLineSegment(sketch, "E667.trimOffspring", {"start": v(-121, 22) * mm, "end": v(-125, 22) * mm});
            skLineSegment(sketch, "E668.trimOffspring", {"start": v(-121, 22) * mm, "end": v(-121, 18) * mm});
            skLineSegment(sketch, "E669.trimOffspring", {"start": v(-121, 23) * mm, "end": v(-125, 23) * mm});
            skLineSegment(sketch, "E670.trimOffspring", {"start": v(-140, 12) * mm, "end": v(-140, 8) * mm});
            skLineSegment(sketch, "E671.trimOffspring", {"start": v(-136, 12) * mm, "end": v(-136, 8) * mm});
            skLineSegment(sketch, "E672.trimOffspring", {"start": v(-135, 12) * mm, "end": v(-135, 8) * mm});
            skLineSegment(sketch, "E673.trimOffspring", {"start": v(-136, 13) * mm, "end": v(-140, 13) * mm});
            skLineSegment(sketch, "E674.trimOffspring", {"start": v(-140, 7) * mm, "end": v(-140, 3) * mm});
            skLineSegment(sketch, "E675.trimOffspring", {"start": v(-135, 3) * mm, "end": v(-131, 3) * mm});
            skLineSegment(sketch, "E676.trimOffspring", {"start": v(-136, 7) * mm, "end": v(-140, 7) * mm});
            skLineSegment(sketch, "E677.trimOffspring", {"start": v(-136, 8) * mm, "end": v(-140, 8) * mm});
            skLineSegment(sketch, "E678.trimOffspring", {"start": v(-136, 7) * mm, "end": v(-136, 3) * mm});
            skLineSegment(sketch, "E679.trimOffspring", {"start": v(-135, 7) * mm, "end": v(-135, 3) * mm});
            skLineSegment(sketch, "E680.trimOffspring", {"start": v(-136, 12) * mm, "end": v(-140, 12) * mm});
            skLineSegment(sketch, "E681.trimOffspring", {"start": v(-131, 12) * mm, "end": v(-135, 12) * mm});
            skLineSegment(sketch, "E682.trimOffspring", {"start": v(-131, 12) * mm, "end": v(-131, 8) * mm});
            skLineSegment(sketch, "E683.trimOffspring", {"start": v(-131, 13) * mm, "end": v(-135, 13) * mm});
            skLineSegment(sketch, "E684.trimOffspring", {"start": v(-130, 12) * mm, "end": v(-130, 8) * mm});
            skLineSegment(sketch, "E685.trimOffspring", {"start": v(-131, 17) * mm, "end": v(-135, 17) * mm});
            skLineSegment(sketch, "E686.trimOffspring", {"start": v(-131, 17) * mm, "end": v(-131, 13) * mm});
            skLineSegment(sketch, "E687.trimOffspring", {"start": v(-131, 18) * mm, "end": v(-135, 18) * mm});
            skLineSegment(sketch, "E688.trimOffspring", {"start": v(-130, 17) * mm, "end": v(-130, 13) * mm});
            skLineSegment(sketch, "E689.trimOffspring", {"start": v(-126, 17) * mm, "end": v(-126, 13) * mm});
            skLineSegment(sketch, "E690.trimOffspring", {"start": v(-126, 17) * mm, "end": v(-130, 17) * mm});
            skLineSegment(sketch, "E691.trimOffspring", {"start": v(-125, 17) * mm, "end": v(-125, 13) * mm});
            skLineSegment(sketch, "E692.trimOffspring", {"start": v(-126, 18) * mm, "end": v(-130, 18) * mm});
            skLineSegment(sketch, "E693.trimOffspring", {"start": v(-121, 18) * mm, "end": v(-125, 18) * mm});
            skLineSegment(sketch, "E694.trimOffspring", {"start": v(-121, 17) * mm, "end": v(-121, 13) * mm});
            skLineSegment(sketch, "E695.trimOffspring", {"start": v(-121, 17) * mm, "end": v(-125, 17) * mm});
            skLineSegment(sketch, "E696.trimOffspring", {"start": v(-120, 17) * mm, "end": v(-120, 13) * mm});
            skLineSegment(sketch, "E697.trimOffspring", {"start": v(-116, 17) * mm, "end": v(-116, 13) * mm});
            skLineSegment(sketch, "E698.trimOffspring", {"start": v(-116, 17) * mm, "end": v(-120, 17) * mm});
            skLineSegment(sketch, "E699.trimOffspring", {"start": v(-115, 17) * mm, "end": v(-115, 13) * mm});
            skLineSegment(sketch, "E700.trimOffspring", {"start": v(-116, 18) * mm, "end": v(-120, 18) * mm});
            skLineSegment(sketch, "E701.trimOffspring", {"start": v(-111, 23) * mm, "end": v(-115, 23) * mm});
            skLineSegment(sketch, "E702.trimOffspring", {"start": v(-111, 22) * mm, "end": v(-115, 22) * mm});
            skLineSegment(sketch, "E703.trimOffspring", {"start": v(-110, 22) * mm, "end": v(-110, 18) * mm});
            skLineSegment(sketch, "E704.trimOffspring", {"start": v(-111, 22) * mm, "end": v(-111, 18) * mm});
            skLineSegment(sketch, "E705.trimOffspring", {"start": v(-106, 22) * mm, "end": v(-106, 18) * mm});
            skLineSegment(sketch, "E706.trimOffspring", {"start": v(-105, 22) * mm, "end": v(-105, 18) * mm});
            skLineSegment(sketch, "E707.trimOffspring", {"start": v(-106, 23) * mm, "end": v(-110, 23) * mm});
            skLineSegment(sketch, "E708.trimOffspring", {"start": v(-106, 22) * mm, "end": v(-110, 22) * mm});
            skLineSegment(sketch, "E709.trimOffspring", {"start": v(-101, 22) * mm, "end": v(-105, 22) * mm});
            skLineSegment(sketch, "E710.trimOffspring", {"start": v(-101, 22) * mm, "end": v(-101, 18) * mm});
            skLineSegment(sketch, "E711.trimOffspring", {"start": v(-101, 23) * mm, "end": v(-105, 23) * mm});
            skLineSegment(sketch, "E712.trimOffspring", {"start": v(-100, 22) * mm, "end": v(-100, 18) * mm});
            skLineSegment(sketch, "E713.trimOffspring", {"start": v(-101, 27) * mm, "end": v(-105, 27) * mm});
            skLineSegment(sketch, "E714.trimOffspring", {"start": v(-101, 27) * mm, "end": v(-101, 23) * mm});
            skLineSegment(sketch, "E715.trimOffspring", {"start": v(-101, 28) * mm, "end": v(-105, 28) * mm});
            skLineSegment(sketch, "E716.trimOffspring", {"start": v(-100, 27) * mm, "end": v(-100, 23) * mm});
            skLineSegment(sketch, "E717.trimOffspring", {"start": v(-101, 32) * mm, "end": v(-105, 32) * mm});
            skLineSegment(sketch, "E718.trimOffspring", {"start": v(-101, 33) * mm, "end": v(-105, 33) * mm});
            skLineSegment(sketch, "E719.trimOffspring", {"start": v(-101, 32) * mm, "end": v(-101, 28) * mm});
            skLineSegment(sketch, "E720.trimOffspring", {"start": v(-100, 32) * mm, "end": v(-100, 28) * mm});
            skLineSegment(sketch, "E721.trimOffspring", {"start": v(-131, 7) * mm, "end": v(-135, 7) * mm});
            skLineSegment(sketch, "E722.trimOffspring", {"start": v(-131, 8) * mm, "end": v(-135, 8) * mm});
            skLineSegment(sketch, "E723.trimOffspring", {"start": v(-131, 7) * mm, "end": v(-131, 3) * mm});
            skLineSegment(sketch, "E724.trimOffspring", {"start": v(-130, 7) * mm, "end": v(-130, 3) * mm});
            skLineSegment(sketch, "E725.trimOffspring", {"start": v(-126, 7) * mm, "end": v(-130, 7) * mm});
            skLineSegment(sketch, "E726.trimOffspring", {"start": v(-126, 8) * mm, "end": v(-130, 8) * mm});
            skLineSegment(sketch, "E727.trimOffspring", {"start": v(-125, 7) * mm, "end": v(-125, 3) * mm});
            skLineSegment(sketch, "E728.trimOffspring", {"start": v(-126, 7) * mm, "end": v(-126, 3) * mm});
            skLineSegment(sketch, "E729.trimOffspring", {"start": v(-126, 12) * mm, "end": v(-130, 12) * mm});
            skLineSegment(sketch, "E730.trimOffspring", {"start": v(-126, 13) * mm, "end": v(-130, 13) * mm});
            skLineSegment(sketch, "E731.trimOffspring", {"start": v(-125, 12) * mm, "end": v(-125, 8) * mm});
            skLineSegment(sketch, "E732.trimOffspring", {"start": v(-126, 12) * mm, "end": v(-126, 8) * mm});
            skLineSegment(sketch, "E733.trimOffspring", {"start": v(-121, 12) * mm, "end": v(-121, 8) * mm});
            skLineSegment(sketch, "E734.trimOffspring", {"start": v(-121, 13) * mm, "end": v(-125, 13) * mm});
            skLineSegment(sketch, "E735.trimOffspring", {"start": v(-121, 12) * mm, "end": v(-125, 12) * mm});
            skLineSegment(sketch, "E736.trimOffspring", {"start": v(-120, 12) * mm, "end": v(-120, 8) * mm});
            skLineSegment(sketch, "E737.trimOffspring", {"start": v(-121, 7) * mm, "end": v(-125, 7) * mm});
            skLineSegment(sketch, "E738.trimOffspring", {"start": v(-121, 7) * mm, "end": v(-121, 3) * mm});
            skLineSegment(sketch, "E739.trimOffspring", {"start": v(-121, 8) * mm, "end": v(-125, 8) * mm});
            skLineSegment(sketch, "E740.trimOffspring", {"start": v(-120, 7) * mm, "end": v(-120, 3) * mm});
            skLineSegment(sketch, "E741.trimOffspring", {"start": v(-116, 7) * mm, "end": v(-116, 3) * mm});
            skLineSegment(sketch, "E742.trimOffspring", {"start": v(-115, 7) * mm, "end": v(-115, 3) * mm});
            skLineSegment(sketch, "E743.trimOffspring", {"start": v(-116, 8) * mm, "end": v(-120, 8) * mm});
            skLineSegment(sketch, "E744.trimOffspring", {"start": v(-116, 7) * mm, "end": v(-120, 7) * mm});
            skLineSegment(sketch, "E745.trimOffspring", {"start": v(-116, 12) * mm, "end": v(-120, 12) * mm});
            skLineSegment(sketch, "E746.trimOffspring", {"start": v(-116, 12) * mm, "end": v(-116, 8) * mm});
            skLineSegment(sketch, "E747.trimOffspring", {"start": v(-116, 13) * mm, "end": v(-120, 13) * mm});
            skLineSegment(sketch, "E748.trimOffspring", {"start": v(-115, 12) * mm, "end": v(-115, 8) * mm});
            skLineSegment(sketch, "E749.trimOffspring", {"start": v(-111, 12) * mm, "end": v(-115, 12) * mm});
            skLineSegment(sketch, "E750.trimOffspring", {"start": v(-110, 12) * mm, "end": v(-110, 8) * mm});
            skLineSegment(sketch, "E751.trimOffspring", {"start": v(-111, 13) * mm, "end": v(-115, 13) * mm});
            skLineSegment(sketch, "E752.trimOffspring", {"start": v(-111, 12) * mm, "end": v(-111, 8) * mm});
            skLineSegment(sketch, "E753.trimOffspring", {"start": v(-111, 17) * mm, "end": v(-115, 17) * mm});
            skLineSegment(sketch, "E754.trimOffspring", {"start": v(-111, 17) * mm, "end": v(-111, 13) * mm});
            skLineSegment(sketch, "E755.trimOffspring", {"start": v(-111, 18) * mm, "end": v(-115, 18) * mm});
            skLineSegment(sketch, "E756.trimOffspring", {"start": v(-110, 17) * mm, "end": v(-110, 13) * mm});
            skLineSegment(sketch, "E757.trimOffspring", {"start": v(-106, 17) * mm, "end": v(-106, 13) * mm});
            skLineSegment(sketch, "E758.trimOffspring", {"start": v(-106, 17) * mm, "end": v(-110, 17) * mm});
            skLineSegment(sketch, "E759.trimOffspring", {"start": v(-105, 17) * mm, "end": v(-105, 13) * mm});
            skLineSegment(sketch, "E760.trimOffspring", {"start": v(-106, 18) * mm, "end": v(-110, 18) * mm});
            skLineSegment(sketch, "E761.trimOffspring", {"start": v(-100, 3) * mm, "end": v(-96, 3) * mm});
            skLineSegment(sketch, "E762.trimOffspring", {"start": v(-90, 3) * mm, "end": v(-86, 3) * mm});
            skLineSegment(sketch, "E763.trimOffspring", {"start": v(-91, 7) * mm, "end": v(-95, 7) * mm});
            skLineSegment(sketch, "E764.trimOffspring", {"start": v(-91, 8) * mm, "end": v(-95, 8) * mm});
            skLineSegment(sketch, "E765.trimOffspring", {"start": v(-90, 7) * mm, "end": v(-90, 3) * mm});
            skLineSegment(sketch, "E766.trimOffspring", {"start": v(-91, 7) * mm, "end": v(-91, 3) * mm});
            skLineSegment(sketch, "E767.trimOffspring", {"start": v(-96, 8) * mm, "end": v(-100, 8) * mm});
            skLineSegment(sketch, "E768.trimOffspring", {"start": v(-96, 7) * mm, "end": v(-96, 3) * mm});
            skLineSegment(sketch, "E769.trimOffspring", {"start": v(-96, 7) * mm, "end": v(-100, 7) * mm});
            skLineSegment(sketch, "E770.trimOffspring", {"start": v(-100, 7) * mm, "end": v(-100, 3) * mm});
            skLineSegment(sketch, "E771.trimOffspring", {"start": v(-101, 8) * mm, "end": v(-105, 8) * mm});
            skLineSegment(sketch, "E772.trimOffspring", {"start": v(-101, 7) * mm, "end": v(-101, 3) * mm});
            skLineSegment(sketch, "E773.trimOffspring", {"start": v(-101, 7) * mm, "end": v(-105, 7) * mm});
            skLineSegment(sketch, "E774.trimOffspring", {"start": v(-105, 7) * mm, "end": v(-105, 3) * mm});
            skLineSegment(sketch, "E775.trimOffspring", {"start": v(-106, 8) * mm, "end": v(-110, 8) * mm});
            skLineSegment(sketch, "E776.trimOffspring", {"start": v(-106, 7) * mm, "end": v(-110, 7) * mm});
            skLineSegment(sketch, "E777.trimOffspring", {"start": v(-110, 7) * mm, "end": v(-110, 3) * mm});
            skLineSegment(sketch, "E778.trimOffspring", {"start": v(-111, 7) * mm, "end": v(-111, 3) * mm});
            skLineSegment(sketch, "E779.trimOffspring", {"start": v(-111, 7) * mm, "end": v(-115, 7) * mm});
            skLineSegment(sketch, "E780.trimOffspring", {"start": v(-111, 8) * mm, "end": v(-115, 8) * mm});
            skLineSegment(sketch, "E781.trimOffspring", {"start": v(-106, 7) * mm, "end": v(-106, 3) * mm});
            skLineSegment(sketch, "E782.trimOffspring", {"start": v(-105, 3) * mm, "end": v(-101, 3) * mm});
            skLineSegment(sketch, "E783.trimOffspring", {"start": v(-110, 3) * mm, "end": v(-106, 3) * mm});
            skLineSegment(sketch, "E784.trimOffspring", {"start": v(-115, 3) * mm, "end": v(-111, 3) * mm});
            skLineSegment(sketch, "E785.trimOffspring", {"start": v(-120, 3) * mm, "end": v(-116, 3) * mm});
            skLineSegment(sketch, "E786.trimOffspring", {"start": v(-125, 3) * mm, "end": v(-121, 3) * mm});
            skLineSegment(sketch, "E787.trimOffspring", {"start": v(-85, 3) * mm, "end": v(-81, 3) * mm});
            skLineSegment(sketch, "E788.trimOffspring", {"start": v(-86, 7) * mm, "end": v(-90, 7) * mm});
            skLineSegment(sketch, "E789.trimOffspring", {"start": v(-86, 8) * mm, "end": v(-90, 8) * mm});
            skLineSegment(sketch, "E790.trimOffspring", {"start": v(-85, 7) * mm, "end": v(-85, 3) * mm});
            skLineSegment(sketch, "E791.trimOffspring", {"start": v(-86, 7) * mm, "end": v(-86, 3) * mm});
            skLineSegment(sketch, "E792.trimOffspring", {"start": v(-80, 7) * mm, "end": v(-80, 3) * mm});
            skLineSegment(sketch, "E793.trimOffspring", {"start": v(-81, 8) * mm, "end": v(-85, 8) * mm});
            skLineSegment(sketch, "E794.trimOffspring", {"start": v(-81, 7) * mm, "end": v(-81, 3) * mm});
            skLineSegment(sketch, "E795.trimOffspring", {"start": v(-81, 7) * mm, "end": v(-85, 7) * mm});
            skLineSegment(sketch, "E796.trimOffspring", {"start": v(-80, 3) * mm, "end": v(-76, 3) * mm});
            skLineSegment(sketch, "E797.trimOffspring", {"start": v(-75, 3) * mm, "end": v(-71, 3) * mm});
            skLineSegment(sketch, "E798.trimOffspring", {"start": v(-95, 22) * mm, "end": v(-95, 18) * mm});
            skLineSegment(sketch, "E799.trimOffspring", {"start": v(-96, 23) * mm, "end": v(-100, 23) * mm});
            skLineSegment(sketch, "E800.trimOffspring", {"start": v(-96, 22) * mm, "end": v(-96, 18) * mm});
            skLineSegment(sketch, "E801.trimOffspring", {"start": v(-96, 22) * mm, "end": v(-100, 22) * mm});
            skLineSegment(sketch, "E802.trimOffspring", {"start": v(-96, 18) * mm, "end": v(-100, 18) * mm});
            skLineSegment(sketch, "E803.trimOffspring", {"start": v(-95, 17) * mm, "end": v(-95, 8) * mm});
            skLineSegment(sketch, "E804.trimOffspring", {"start": v(-96, 17) * mm, "end": v(-96, 13) * mm});
            skLineSegment(sketch, "E805.trimOffspring", {"start": v(-96, 17) * mm, "end": v(-100, 17) * mm});
            skLineSegment(sketch, "E806.trimOffspring", {"start": v(-100, 17) * mm, "end": v(-100, 13) * mm});
            skLineSegment(sketch, "E807.trimOffspring", {"start": v(-101, 18) * mm, "end": v(-105, 18) * mm});
            skLineSegment(sketch, "E808.trimOffspring", {"start": v(-101, 17) * mm, "end": v(-101, 13) * mm});
            skLineSegment(sketch, "E809.trimOffspring", {"start": v(-101, 17) * mm, "end": v(-105, 17) * mm});
            skLineSegment(sketch, "E810.trimOffspring", {"start": v(-101, 13) * mm, "end": v(-105, 13) * mm});
            skLineSegment(sketch, "E811.trimOffspring", {"start": v(-100, 12) * mm, "end": v(-100, 8) * mm});
            skLineSegment(sketch, "E812.trimOffspring", {"start": v(-101, 12) * mm, "end": v(-101, 8) * mm});
            skLineSegment(sketch, "E813.trimOffspring", {"start": v(-101, 12) * mm, "end": v(-105, 12) * mm});
            skLineSegment(sketch, "E814.trimOffspring", {"start": v(-105, 12) * mm, "end": v(-105, 8) * mm});
            skLineSegment(sketch, "E815.trimOffspring", {"start": v(-106, 13) * mm, "end": v(-110, 13) * mm});
            skLineSegment(sketch, "E816.trimOffspring", {"start": v(-106, 12) * mm, "end": v(-106, 8) * mm});
            skLineSegment(sketch, "E817.trimOffspring", {"start": v(-106, 12) * mm, "end": v(-110, 12) * mm});
            skLineSegment(sketch, "E818.trimOffspring", {"start": v(-91, 17) * mm, "end": v(-95, 17) * mm});
            skLineSegment(sketch, "E819.trimOffspring", {"start": v(-90, 17) * mm, "end": v(-90, 13) * mm});
            skLineSegment(sketch, "E820.trimOffspring", {"start": v(-91, 18) * mm, "end": v(-95, 18) * mm});
            skLineSegment(sketch, "E821.trimOffspring", {"start": v(-91, 17) * mm, "end": v(-91, 13) * mm});
            skLineSegment(sketch, "E822.trimOffspring", {"start": v(-91, 22) * mm, "end": v(-95, 22) * mm});
            skLineSegment(sketch, "E823.trimOffspring", {"start": v(-91, 23) * mm, "end": v(-95, 23) * mm});
            skLineSegment(sketch, "E824.trimOffspring", {"start": v(-90, 22) * mm, "end": v(-90, 18) * mm});
            skLineSegment(sketch, "E825.trimOffspring", {"start": v(-96, 27) * mm, "end": v(-100, 27) * mm});
            skLineSegment(sketch, "E826.trimOffspring", {"start": v(-96, 27) * mm, "end": v(-96, 23) * mm});
            skLineSegment(sketch, "E827.trimOffspring", {"start": v(-96, 28) * mm, "end": v(-100, 28) * mm});
            skLineSegment(sketch, "E828.trimOffspring", {"start": v(-95, 27) * mm, "end": v(-95, 23) * mm});
            skLineSegment(sketch, "E829.trimOffspring", {"start": v(-91, 27) * mm, "end": v(-91, 23) * mm});
            skLineSegment(sketch, "E830.trimOffspring", {"start": v(-91, 27) * mm, "end": v(-95, 27) * mm});
            skLineSegment(sketch, "E831.trimOffspring", {"start": v(-90, 27) * mm, "end": v(-90, 23) * mm});
            skLineSegment(sketch, "E832.trimOffspring", {"start": v(-91, 28) * mm, "end": v(-95, 28) * mm});
            skLineSegment(sketch, "E833", {"start": v(-91, 22) * mm, "end": v(-91, 18) * mm});
            skLineSegment(sketch, "E834", {"start": v(-90, 18) * mm, "end": v(-86, 18) * mm});
            skLineSegment(sketch, "E835", {"start": v(-86, 27) * mm, "end": v(-90, 27) * mm});
            skLineSegment(sketch, "E836.trimOffspring", {"start": v(-85, 17) * mm, "end": v(-85, 13) * mm});
            skLineSegment(sketch, "E837.trimOffspring", {"start": v(-86, 17) * mm, "end": v(-86, 13) * mm});
            skLineSegment(sketch, "E838.trimOffspring", {"start": v(-86, 17) * mm, "end": v(-90, 17) * mm});
            skLineSegment(sketch, "E839.trimOffspring", {"start": v(-86, 22) * mm, "end": v(-90, 22) * mm});
            skLineSegment(sketch, "E840.trimOffspring", {"start": v(-86, 22) * mm, "end": v(-86, 18) * mm});
            skLineSegment(sketch, "E841.trimOffspring", {"start": v(-86, 23) * mm, "end": v(-90, 23) * mm});
            skLineSegment(sketch, "E842.trimOffspring", {"start": v(-85, 22) * mm, "end": v(-85, 18) * mm});
            skLineSegment(sketch, "E843.trimOffspring", {"start": v(-86, 27) * mm, "end": v(-86, 23) * mm});
            skLineSegment(sketch, "E844.trimOffspring", {"start": v(-86, 28) * mm, "end": v(-90, 28) * mm});
            skLineSegment(sketch, "E845.trimOffspring", {"start": v(-85, 27) * mm, "end": v(-85, 23) * mm});
            skLineSegment(sketch, "E846.trimOffspring", {"start": v(-86, 12) * mm, "end": v(-90, 12) * mm});
            skLineSegment(sketch, "E847.trimOffspring", {"start": v(-86, 12) * mm, "end": v(-86, 8) * mm});
            skLineSegment(sketch, "E848.trimOffspring", {"start": v(-86, 13) * mm, "end": v(-90, 13) * mm});
            skLineSegment(sketch, "E849.trimOffspring", {"start": v(-85, 12) * mm, "end": v(-85, 8) * mm});
            skLineSegment(sketch, "E850.trimOffspring", {"start": v(-90, 12) * mm, "end": v(-90, 8) * mm});
            skLineSegment(sketch, "E851.trimOffspring", {"start": v(-91, 13) * mm, "end": v(-95, 13) * mm});
            skLineSegment(sketch, "E852.trimOffspring", {"start": v(-91, 12) * mm, "end": v(-91, 8) * mm});
            skLineSegment(sketch, "E853.trimOffspring", {"start": v(-91, 12) * mm, "end": v(-95, 12) * mm});
            skLineSegment(sketch, "E854.trimOffspring", {"start": v(-96, 12) * mm, "end": v(-100, 12) * mm});
            skLineSegment(sketch, "E855.trimOffspring", {"start": v(-96, 12) * mm, "end": v(-96, 8) * mm});
            skLineSegment(sketch, "E856.trimOffspring", {"start": v(-96, 13) * mm, "end": v(-100, 13) * mm});
            skLineSegment(sketch, "E857.trimOffspring", {"start": v(-76, 7) * mm, "end": v(-80, 7) * mm});
            skLineSegment(sketch, "E858.trimOffspring", {"start": v(-76, 8) * mm, "end": v(-80, 8) * mm});
            skLineSegment(sketch, "E859.trimOffspring", {"start": v(-75, 7) * mm, "end": v(-75, 3) * mm});
            skLineSegment(sketch, "E860.trimOffspring", {"start": v(-76, 7) * mm, "end": v(-76, 3) * mm});
            skLineSegment(sketch, "E861.trimOffspring", {"start": v(-80, 12) * mm, "end": v(-80, 8) * mm});
            skLineSegment(sketch, "E862.trimOffspring", {"start": v(-81, 12) * mm, "end": v(-81, 8) * mm});
            skLineSegment(sketch, "E863.trimOffspring", {"start": v(-81, 13) * mm, "end": v(-85, 13) * mm});
            skLineSegment(sketch, "E864.trimOffspring", {"start": v(-81, 12) * mm, "end": v(-85, 12) * mm});
            skLineSegment(sketch, "E865.trimOffspring", {"start": v(-80, 17) * mm, "end": v(-80, 13) * mm});
            skLineSegment(sketch, "E866.trimOffspring", {"start": v(-81, 18) * mm, "end": v(-85, 18) * mm});
            skLineSegment(sketch, "E867.trimOffspring", {"start": v(-81, 17) * mm, "end": v(-81, 13) * mm});
            skLineSegment(sketch, "E868.trimOffspring", {"start": v(-81, 17) * mm, "end": v(-85, 17) * mm});
            skLineSegment(sketch, "E869.trimOffspring", {"start": v(-81, 22) * mm, "end": v(-81, 18) * mm});
            skLineSegment(sketch, "E870.trimOffspring", {"start": v(-81, 23) * mm, "end": v(-85, 23) * mm});
            skLineSegment(sketch, "E871.trimOffspring", {"start": v(-80, 22) * mm, "end": v(-80, 18) * mm});
            skLineSegment(sketch, "E872.trimOffspring", {"start": v(-81, 22) * mm, "end": v(-85, 22) * mm});
            skLineSegment(sketch, "E873.trimOffspring", {"start": v(-81, 27) * mm, "end": v(-85, 27) * mm});
            skLineSegment(sketch, "E874.trimOffspring", {"start": v(-81, 27) * mm, "end": v(-81, 23) * mm});
            skLineSegment(sketch, "E875.trimOffspring", {"start": v(-80, 27) * mm, "end": v(-80, 23) * mm});
            skLineSegment(sketch, "E876.trimOffspring", {"start": v(-81, 28) * mm, "end": v(-85, 28) * mm});
            skLineSegment(sketch, "E877.trimOffspring", {"start": v(-76, 17) * mm, "end": v(-76, 13) * mm});
            skLineSegment(sketch, "E878.trimOffspring", {"start": v(-76, 18) * mm, "end": v(-80, 18) * mm});
            skLineSegment(sketch, "E879.trimOffspring", {"start": v(-75, 17) * mm, "end": v(-75, 13) * mm});
            skLineSegment(sketch, "E880.trimOffspring", {"start": v(-76, 17) * mm, "end": v(-80, 17) * mm});
            skLineSegment(sketch, "E881.trimOffspring", {"start": v(-95, 3) * mm, "end": v(-91, 3) * mm});
            skLineSegment(sketch, "E882", {"start": v(-95, 7) * mm, "end": v(-95, 3) * mm});
            skLineSegment(sketch, "E883.trimOffspring", {"start": v(-100, 36.5) * mm, "end": v(-96, 36.5) * mm});
            skLineSegment(sketch, "E884.trimOffspring", {"start": v(-96, 33) * mm, "end": v(-100, 33) * mm});
            skLineSegment(sketch, "E885.trimOffspring", {"start": v(-96, 32) * mm, "end": v(-96, 28) * mm});
            skLineSegment(sketch, "E886.trimOffspring", {"start": v(-95, 32) * mm, "end": v(-95, 28) * mm});
            skLineSegment(sketch, "E887.trimOffspring", {"start": v(-96, 32) * mm, "end": v(-100, 32) * mm});
            skLineSegment(sketch, "E888.trimOffspring", {"start": v(-90, 32) * mm, "end": v(-90, 28) * mm});
            skLineSegment(sketch, "E889.trimOffspring", {"start": v(-91, 33) * mm, "end": v(-95, 33) * mm});
            skLineSegment(sketch, "E890.trimOffspring", {"start": v(-90, 36.5) * mm, "end": v(-86, 36.5) * mm});
            skLineSegment(sketch, "E891", {"start": v(-95, 36.5) * mm, "end": v(-91, 36.5) * mm});
            skLineSegment(sketch, "E892", {"start": v(-91, 28) * mm, "end": v(-91, 32) * mm});
            skLineSegment(sketch, "E893", {"start": v(-91, 32) * mm, "end": v(-95, 32) * mm});
            skLineSegment(sketch, "E894.trimOffspring", {"start": v(-85, 36.5) * mm, "end": v(-81, 36.5) * mm});
            skLineSegment(sketch, "E895.trimOffspring", {"start": v(-80, 36.5) * mm, "end": v(-76, 36.5) * mm});
            skLineSegment(sketch, "E896.trimOffspring", {"start": v(-81, 32) * mm, "end": v(-90, 32) * mm});
            skLineSegment(sketch, "E897.trimOffspring", {"start": v(-80, 32) * mm, "end": v(-80, 28) * mm});
            skLineSegment(sketch, "E898.trimOffspring", {"start": v(-81, 33) * mm, "end": v(-90, 33) * mm});
            skLineSegment(sketch, "E899.trimOffspring", {"start": v(-81, 32) * mm, "end": v(-81, 28) * mm});
            skLineSegment(sketch, "E900.trimOffspring", {"start": v(-85, 32) * mm, "end": v(-85, 28) * mm});
            skLineSegment(sketch, "E901.trimOffspring", {"start": v(-86, 32) * mm, "end": v(-86, 28) * mm});
            skLineSegment(sketch, "E902.trimOffspring", {"start": v(-76, 27) * mm, "end": v(-80, 27) * mm});
            skLineSegment(sketch, "E903.trimOffspring", {"start": v(-76, 27) * mm, "end": v(-76, 23) * mm});
            skLineSegment(sketch, "E904.trimOffspring", {"start": v(-76, 28) * mm, "end": v(-80, 28) * mm});
            skLineSegment(sketch, "E905.trimOffspring", {"start": v(-75, 27) * mm, "end": v(-75, 23) * mm});
            skLineSegment(sketch, "E906.trimOffspring", {"start": v(-76, 32) * mm, "end": v(-80, 32) * mm});
            skLineSegment(sketch, "E907.trimOffspring", {"start": v(-76, 32) * mm, "end": v(-76, 28) * mm});
            skLineSegment(sketch, "E908.trimOffspring", {"start": v(-76, 33) * mm, "end": v(-80, 33) * mm});
            skLineSegment(sketch, "E909.trimOffspring", {"start": v(-75, 32) * mm, "end": v(-75, 28) * mm});
            skLineSegment(sketch, "E910.trimOffspring", {"start": v(-71, 32) * mm, "end": v(-71, 28) * mm});
            skLineSegment(sketch, "E911.trimOffspring", {"start": v(-71, 33) * mm, "end": v(-75, 33) * mm});
            skLineSegment(sketch, "E912.trimOffspring", {"start": v(-70, 32) * mm, "end": v(-70, 28) * mm});
            skLineSegment(sketch, "E913.trimOffspring", {"start": v(-71, 32) * mm, "end": v(-75, 32) * mm});
            skLineSegment(sketch, "E914.trimOffspring", {"start": v(-71, 28) * mm, "end": v(-75, 28) * mm});
            skLineSegment(sketch, "E915.trimOffspring", {"start": v(-71, 27) * mm, "end": v(-75, 27) * mm});
            skLineSegment(sketch, "E916.trimOffspring", {"start": v(-66, 27) * mm, "end": v(-70, 27) * mm});
            skLineSegment(sketch, "E917.trimOffspring", {"start": v(-66, 27) * mm, "end": v(-66, 23) * mm});
            skLineSegment(sketch, "E918.trimOffspring", {"start": v(-65, 27) * mm, "end": v(-65, 23) * mm});
            skLineSegment(sketch, "E919.trimOffspring", {"start": v(-66, 28) * mm, "end": v(-70, 28) * mm});
            skLineSegment(sketch, "E920.trimOffspring", {"start": v(-61, 27) * mm, "end": v(-61, 23) * mm});
            skLineSegment(sketch, "E921.trimOffspring", {"start": v(-61, 28) * mm, "end": v(-65, 28) * mm});
            skLineSegment(sketch, "E922.trimOffspring", {"start": v(-60, 27) * mm, "end": v(-60, 23) * mm});
            skLineSegment(sketch, "E923.trimOffspring", {"start": v(-61, 27) * mm, "end": v(-65, 27) * mm});
            skLineSegment(sketch, "E924.trimOffspring", {"start": v(-61, 32) * mm, "end": v(-65, 32) * mm});
            skLineSegment(sketch, "E925.trimOffspring", {"start": v(-61, 32) * mm, "end": v(-61, 28) * mm});
            skLineSegment(sketch, "E926.trimOffspring", {"start": v(-61, 33) * mm, "end": v(-65, 33) * mm});
            skLineSegment(sketch, "E927.trimOffspring", {"start": v(-60, 32) * mm, "end": v(-60, 28) * mm});
            skLineSegment(sketch, "E928.trimOffspring", {"start": v(-60, 36.5) * mm, "end": v(-56, 36.5) * mm});
            skLineSegment(sketch, "E929.trimOffspring", {"start": v(-65, 36.5) * mm, "end": v(-61, 36.5) * mm});
            skLineSegment(sketch, "E930", {"start": v(-75, 36.5) * mm, "end": v(-71, 36.5) * mm});
            skLineSegment(sketch, "E931", {"start": v(-71, 36.5) * mm, "end": v(-71, 33) * mm});
            skLineSegment(sketch, "E932", {"start": v(-70, 33) * mm, "end": v(-70, 36.5) * mm});
            skLineSegment(sketch, "E933", {"start": v(-70, 36.5) * mm, "end": v(-66, 36.5) * mm});
            skLineSegment(sketch, "E934.trimOffspring", {"start": v(-66, 32) * mm, "end": v(-66, 28) * mm});
            skLineSegment(sketch, "E935.trimOffspring", {"start": v(-66, 33) * mm, "end": v(-70, 33) * mm});
            skLineSegment(sketch, "E936.trimOffspring", {"start": v(-66, 32) * mm, "end": v(-70, 32) * mm});
            skLineSegment(sketch, "E937", {"start": v(-66, 36.5) * mm, "end": v(-66, 33) * mm});
            skLineSegment(sketch, "E938", {"start": v(-65, 32) * mm, "end": v(-65, 28) * mm});
            skLineSegment(sketch, "E939.trimOffspring", {"start": v(-55, 27) * mm, "end": v(-55, 23) * mm});
            skLineSegment(sketch, "E940.trimOffspring", {"start": v(-56, 28) * mm, "end": v(-60, 28) * mm});
            skLineSegment(sketch, "E941.trimOffspring", {"start": v(-56, 27) * mm, "end": v(-56, 23) * mm});
            skLineSegment(sketch, "E942.trimOffspring", {"start": v(-56, 27) * mm, "end": v(-60, 27) * mm});
            skLineSegment(sketch, "E943.trimOffspring", {"start": v(-56, 32) * mm, "end": v(-56, 28) * mm});
            skLineSegment(sketch, "E944.trimOffspring", {"start": v(-56, 33) * mm, "end": v(-60, 33) * mm});
            skLineSegment(sketch, "E945.trimOffspring", {"start": v(-55, 32) * mm, "end": v(-55, 28) * mm});
            skLineSegment(sketch, "E946.trimOffspring", {"start": v(-56, 32) * mm, "end": v(-60, 32) * mm});
            skLineSegment(sketch, "E947.trimOffspring", {"start": v(-55, 36.5) * mm, "end": v(-51, 36.5) * mm});
            skLineSegment(sketch, "E948", {"start": v(-56, 36.5) * mm, "end": v(-56, 33) * mm});
            skLineSegment(sketch, "E949.trimOffspring", {"start": v(-76, 22) * mm, "end": v(-76, 18) * mm});
            skLineSegment(sketch, "E950.trimOffspring", {"start": v(-76, 23) * mm, "end": v(-80, 23) * mm});
            skLineSegment(sketch, "E951.trimOffspring", {"start": v(-75, 22) * mm, "end": v(-75, 18) * mm});
            skLineSegment(sketch, "E952.trimOffspring", {"start": v(-76, 22) * mm, "end": v(-80, 22) * mm});
            skLineSegment(sketch, "E953.trimOffspring", {"start": v(-75, 12) * mm, "end": v(-75, 8) * mm});
            skLineSegment(sketch, "E954.trimOffspring", {"start": v(-76, 13) * mm, "end": v(-80, 13) * mm});
            skLineSegment(sketch, "E955.trimOffspring", {"start": v(-76, 12) * mm, "end": v(-76, 8) * mm});
            skLineSegment(sketch, "E956.trimOffspring", {"start": v(-76, 12) * mm, "end": v(-80, 12) * mm});
            skLineSegment(sketch, "E957.trimOffspring", {"start": v(-66, 22) * mm, "end": v(-66, 18) * mm});
            skLineSegment(sketch, "E958.trimOffspring", {"start": v(-66, 23) * mm, "end": v(-70, 23) * mm});
            skLineSegment(sketch, "E959.trimOffspring", {"start": v(-65, 22) * mm, "end": v(-65, 18) * mm});
            skLineSegment(sketch, "E960.trimOffspring", {"start": v(-66, 22) * mm, "end": v(-70, 22) * mm});
            skLineSegment(sketch, "E961.trimOffspring", {"start": v(-70, 22) * mm, "end": v(-70, 18) * mm});
            skLineSegment(sketch, "E962.trimOffspring", {"start": v(-71, 23) * mm, "end": v(-75, 23) * mm});
            skLineSegment(sketch, "E963.trimOffspring", {"start": v(-71, 22) * mm, "end": v(-71, 18) * mm});
            skLineSegment(sketch, "E964.trimOffspring", {"start": v(-71, 22) * mm, "end": v(-75, 22) * mm});
            skLineSegment(sketch, "E965.trimOffspring", {"start": v(-60, 22) * mm, "end": v(-60, 18) * mm});
            skLineSegment(sketch, "E966.trimOffspring", {"start": v(-61, 23) * mm, "end": v(-65, 23) * mm});
            skLineSegment(sketch, "E967.trimOffspring", {"start": v(-61, 22) * mm, "end": v(-61, 18) * mm});
            skLineSegment(sketch, "E968.trimOffspring", {"start": v(-61, 22) * mm, "end": v(-65, 22) * mm});
            skLineSegment(sketch, "E969.trimOffspring", {"start": v(-60, 17) * mm, "end": v(-60, 13) * mm});
            skLineSegment(sketch, "E970.trimOffspring", {"start": v(-61, 18) * mm, "end": v(-65, 18) * mm});
            skLineSegment(sketch, "E971.trimOffspring", {"start": v(-61, 17) * mm, "end": v(-61, 13) * mm});
            skLineSegment(sketch, "E972.trimOffspring", {"start": v(-65, 17) * mm, "end": v(-65, 13) * mm});
            skLineSegment(sketch, "E973.trimOffspring", {"start": v(-66, 18) * mm, "end": v(-70, 18) * mm});
            skLineSegment(sketch, "E974.trimOffspring", {"start": v(-66, 17) * mm, "end": v(-66, 13) * mm});
            skLineSegment(sketch, "E975.trimOffspring", {"start": v(-66, 17) * mm, "end": v(-70, 17) * mm});
            skLineSegment(sketch, "E976.trimOffspring", {"start": v(-70, 17) * mm, "end": v(-70, 13) * mm});
            skLineSegment(sketch, "E977.trimOffspring", {"start": v(-71, 18) * mm, "end": v(-75, 18) * mm});
            skLineSegment(sketch, "E978.trimOffspring", {"start": v(-71, 17) * mm, "end": v(-71, 13) * mm});
            skLineSegment(sketch, "E979.trimOffspring", {"start": v(-71, 17) * mm, "end": v(-75, 17) * mm});
            skLineSegment(sketch, "E980.trimOffspring", {"start": v(-71, 12) * mm, "end": v(-71, 8) * mm});
            skLineSegment(sketch, "E981.trimOffspring", {"start": v(-70, 12) * mm, "end": v(-70, 8) * mm});
            skLineSegment(sketch, "E982.trimOffspring", {"start": v(-71, 13) * mm, "end": v(-75, 13) * mm});
            skLineSegment(sketch, "E983.trimOffspring", {"start": v(-71, 12) * mm, "end": v(-75, 12) * mm});
            skLineSegment(sketch, "E984.trimOffspring", {"start": v(-71, 8) * mm, "end": v(-75, 8) * mm});
            skLineSegment(sketch, "E985.trimOffspring", {"start": v(-71, 7) * mm, "end": v(-71, 3) * mm});
            skLineSegment(sketch, "E986.trimOffspring", {"start": v(-70, 7) * mm, "end": v(-70, 3) * mm});
            skLineSegment(sketch, "E987.trimOffspring", {"start": v(-71, 7) * mm, "end": v(-75, 7) * mm});
            skLineSegment(sketch, "E988", {"start": v(-65, 17) * mm, "end": v(-61, 17) * mm});
            skLineSegment(sketch, "E989.trimOffspring", {"start": v(-56, 22) * mm, "end": v(-56, 18) * mm});
            skLineSegment(sketch, "E990.trimOffspring", {"start": v(-56, 23) * mm, "end": v(-60, 23) * mm});
            skLineSegment(sketch, "E991.trimOffspring", {"start": v(-55, 22) * mm, "end": v(-55, 18) * mm});
            skLineSegment(sketch, "E992.trimOffspring", {"start": v(-56, 22) * mm, "end": v(-60, 22) * mm});
            skLineSegment(sketch, "E993.trimOffspring", {"start": v(-56, 18) * mm, "end": v(-60, 18) * mm});
            skLineSegment(sketch, "E994.trimOffspring", {"start": v(-56, 17) * mm, "end": v(-56, 13) * mm});
            skLineSegment(sketch, "E995.trimOffspring", {"start": v(-56, 17) * mm, "end": v(-60, 17) * mm});
            skLineSegment(sketch, "E996.trimOffspring", {"start": v(-55, 17) * mm, "end": v(-55, 13) * mm});
            skLineSegment(sketch, "E997.trimOffspring", {"start": v(-56, 7) * mm, "end": v(-60, 7) * mm});
            skLineSegment(sketch, "E998.trimOffspring", {"start": v(-56, 8) * mm, "end": v(-60, 8) * mm});
            skLineSegment(sketch, "E999.trimOffspring", {"start": v(-55, 7) * mm, "end": v(-55, 3) * mm});
            skLineSegment(sketch, "E1000.trimOffspring", {"start": v(-56, 7) * mm, "end": v(-56, 3) * mm});
            skLineSegment(sketch, "E1001.trimOffspring", {"start": v(-55, 12) * mm, "end": v(-55, 8) * mm});
            skLineSegment(sketch, "E1002.trimOffspring", {"start": v(-56, 13) * mm, "end": v(-60, 13) * mm});
            skLineSegment(sketch, "E1003.trimOffspring", {"start": v(-56, 12) * mm, "end": v(-56, 8) * mm});
            skLineSegment(sketch, "E1004.trimOffspring", {"start": v(-56, 12) * mm, "end": v(-60, 12) * mm});
            skLineSegment(sketch, "E1005.trimOffspring", {"start": v(-60, 12) * mm, "end": v(-60, 8) * mm});
            skLineSegment(sketch, "E1006.trimOffspring", {"start": v(-61, 13) * mm, "end": v(-65, 13) * mm});
            skLineSegment(sketch, "E1007.trimOffspring", {"start": v(-61, 12) * mm, "end": v(-61, 8) * mm});
            skLineSegment(sketch, "E1008.trimOffspring", {"start": v(-61, 12) * mm, "end": v(-65, 12) * mm});
            skLineSegment(sketch, "E1009.trimOffspring", {"start": v(-60, 7) * mm, "end": v(-60, 3) * mm});
            skLineSegment(sketch, "E1010.trimOffspring", {"start": v(-61, 8) * mm, "end": v(-65, 8) * mm});
            skLineSegment(sketch, "E1011.trimOffspring", {"start": v(-61, 7) * mm, "end": v(-61, 3) * mm});
            skLineSegment(sketch, "E1012.trimOffspring", {"start": v(-61, 7) * mm, "end": v(-65, 7) * mm});
            skLineSegment(sketch, "E1013.trimOffspring", {"start": v(-65, 7) * mm, "end": v(-65, 3) * mm});
            skLineSegment(sketch, "E1014.trimOffspring", {"start": v(-66, 8) * mm, "end": v(-70, 8) * mm});
            skLineSegment(sketch, "E1015.trimOffspring", {"start": v(-66, 7) * mm, "end": v(-66, 3) * mm});
            skLineSegment(sketch, "E1016.trimOffspring", {"start": v(-66, 7) * mm, "end": v(-70, 7) * mm});
            skLineSegment(sketch, "E1017.trimOffspring", {"start": v(-70, 3) * mm, "end": v(-66, 3) * mm});
            skLineSegment(sketch, "E1018.trimOffspring", {"start": v(-65, 3) * mm, "end": v(-61, 3) * mm});
            skLineSegment(sketch, "E1019.trimOffspring", {"start": v(-60, 3) * mm, "end": v(-56, 3) * mm});
            skLineSegment(sketch, "E1020.trimOffspring", {"start": v(-51, 7) * mm, "end": v(-51, 3) * mm});
            skLineSegment(sketch, "E1021.trimOffspring", {"start": v(-55, 3) * mm, "end": v(-51, 3) * mm});
            skLineSegment(sketch, "E1022.trimOffspring", {"start": v(-51, 17) * mm, "end": v(-51, 13) * mm});
            skLineSegment(sketch, "E1023", {"start": v(-55, 12) * mm, "end": v(-51, 12) * mm});
            skLineSegment(sketch, "E1024", {"start": v(-51, 12) * mm, "end": v(-51, 8) * mm});
            skLineSegment(sketch, "E1025.trimOffspring", {"start": v(-51, 22) * mm, "end": v(-51, 18) * mm});
            skLineSegment(sketch, "E1026.trimOffspring", {"start": v(-51, 27) * mm, "end": v(-51, 23) * mm});
            skLineSegment(sketch, "E1027.trimOffspring", {"start": v(-51, 32) * mm, "end": v(-51, 28) * mm});
            skLineSegment(sketch, "E1028.trimOffspring", {"start": v(-140, 22) * mm, "end": v(-140, 18) * mm});
            skLineSegment(sketch, "E1029.trimOffspring", {"start": v(-50.5, 8) * mm, "end": v(-50.5, 7) * mm});
            skLineSegment(sketch, "E1030.trimOffspring", {"start": v(-50.5, 13) * mm, "end": v(-50.5, 12) * mm});
            skLineSegment(sketch, "E1031.trimOffspring", {"start": v(-50.5, 18) * mm, "end": v(-50.5, 17) * mm});
            skPoint(sketch, "E1032", {"position": v(-96, 36.5) * mm});
            skLineSegment(sketch, "E1033.trimOffspring", {"start": v(-70, 27) * mm, "end": v(-70, 23) * mm});
            skLineSegment(sketch, "E1034.trimOffspring", {"start": v(-71, 27) * mm, "end": v(-71, 23) * mm});
            skLineSegment(sketch, "E1035.trimOffspring", {"start": v(-65, 12) * mm, "end": v(-65, 8) * mm});
            skLineSegment(sketch, "E1036.trimOffspring", {"start": v(-66, 13) * mm, "end": v(-70, 13) * mm});
            skLineSegment(sketch, "E1037.trimOffspring", {"start": v(-66, 12) * mm, "end": v(-66, 8) * mm});
            skLineSegment(sketch, "E1038.trimOffspring", {"start": v(-66, 12) * mm, "end": v(-70, 12) * mm});
            skLineSegment(sketch, "E1039", {"start": v(-46, 0) * mm, "end": v(-51, 0) * mm});
            skLineSegment(sketch, "E1040", {"start": v(-51, 0) * mm, "end": v(-51, 3) * mm});
            skLineSegment(sketch, "E1041.trimOffspring", {"start": v(-130, 3) * mm, "end": v(-126, 3) * mm});
            skLineSegment(sketch, "E1042", {"start": v(-145, 0) * mm, "end": v(-140, 0) * mm});
            skLineSegment(sketch, "E1043", {"start": v(-140, 0) * mm, "end": v(-140, 3) * mm});
            skLineSegment(sketch, "E1044", {"start": v(-140, 28) * mm, "end": v(-140, 32) * mm});
            skLineSegment(sketch, "E1045", {"start": v(-140, 32) * mm, "end": v(-136, 32) * mm});
            skLineSegment(sketch, "E1046", {"start": v(-130, 28) * mm, "end": v(-130, 32) * mm});
            skLineSegment(sketch, "E1047", {"start": v(-130, 36.5) * mm, "end": v(-130, 37.5) * mm});
            skLineSegment(sketch, "E1048.bottom", {"start": v(-130, 37.5) * mm, "end": v(-126, 37.5) * mm});
            skLineSegment(sketch, "E1048.top", {"start": v(-130, 41.5) * mm, "end": v(-126, 41.5) * mm});
            skLineSegment(sketch, "E1048.left", {"start": v(-130, 37.5) * mm, "end": v(-130, 41.5) * mm});
            skLineSegment(sketch, "E1048.right", {"start": v(-126, 37.5) * mm, "end": v(-126, 41.5) * mm});
            skLineSegment(sketch, "E1049.bottom", {"start": v(-125, 37.5) * mm, "end": v(-121, 37.5) * mm});
            skLineSegment(sketch, "E1049.top", {"start": v(-125, 41.5) * mm, "end": v(-121, 41.5) * mm});
            skLineSegment(sketch, "E1049.left", {"start": v(-125, 37.5) * mm, "end": v(-125, 41.5) * mm});
            skLineSegment(sketch, "E1049.right", {"start": v(-121, 37.5) * mm, "end": v(-121, 41.5) * mm});
            skLineSegment(sketch, "E1050.bottom", {"start": v(-120, 37.5) * mm, "end": v(-116, 37.5) * mm});
            skLineSegment(sketch, "E1050.top", {"start": v(-120, 41.5) * mm, "end": v(-116, 41.5) * mm});
            skLineSegment(sketch, "E1050.left", {"start": v(-120, 37.5) * mm, "end": v(-120, 41.5) * mm});
            skLineSegment(sketch, "E1050.right", {"start": v(-116, 37.5) * mm, "end": v(-116, 41.5) * mm});
            skLineSegment(sketch, "E1051.bottom", {"start": v(-115, 37.5) * mm, "end": v(-111, 37.5) * mm});
            skLineSegment(sketch, "E1051.top", {"start": v(-115, 41.5) * mm, "end": v(-111, 41.5) * mm});
            skLineSegment(sketch, "E1051.left", {"start": v(-115, 37.5) * mm, "end": v(-115, 41.5) * mm});
            skLineSegment(sketch, "E1051.right", {"start": v(-111, 37.5) * mm, "end": v(-111, 41.5) * mm});
            skLineSegment(sketch, "E1052.bottom", {"start": v(-110, 37.5) * mm, "end": v(-106, 37.5) * mm});
            skLineSegment(sketch, "E1052.top", {"start": v(-110, 41.5) * mm, "end": v(-106, 41.5) * mm});
            skLineSegment(sketch, "E1052.left", {"start": v(-110, 37.5) * mm, "end": v(-110, 41.5) * mm});
            skLineSegment(sketch, "E1052.right", {"start": v(-106, 37.5) * mm, "end": v(-106, 41.5) * mm});
            skLineSegment(sketch, "E1053.bottom", {"start": v(-105, 37.5) * mm, "end": v(-101, 37.5) * mm});
            skLineSegment(sketch, "E1053.top", {"start": v(-105, 41.5) * mm, "end": v(-101, 41.5) * mm});
            skLineSegment(sketch, "E1053.left", {"start": v(-105, 37.5) * mm, "end": v(-105, 41.5) * mm});
            skLineSegment(sketch, "E1053.right", {"start": v(-101, 37.5) * mm, "end": v(-101, 41.5) * mm});
            skLineSegment(sketch, "E1054.bottom", {"start": v(-100, 37.5) * mm, "end": v(-96, 37.5) * mm});
            skLineSegment(sketch, "E1054.top", {"start": v(-100, 41.5) * mm, "end": v(-96, 41.5) * mm});
            skLineSegment(sketch, "E1054.left", {"start": v(-100, 37.5) * mm, "end": v(-100, 41.5) * mm});
            skLineSegment(sketch, "E1054.right", {"start": v(-96, 37.5) * mm, "end": v(-96, 41.5) * mm});
            skLineSegment(sketch, "E1055.bottom", {"start": v(-95, 37.5) * mm, "end": v(-91, 37.5) * mm});
            skLineSegment(sketch, "E1055.top", {"start": v(-95, 41.5) * mm, "end": v(-91, 41.5) * mm});
            skLineSegment(sketch, "E1055.left", {"start": v(-95, 37.5) * mm, "end": v(-95, 41.5) * mm});
            skLineSegment(sketch, "E1055.right", {"start": v(-91, 37.5) * mm, "end": v(-91, 41.5) * mm});
            skLineSegment(sketch, "E1056.bottom", {"start": v(-90, 37.5) * mm, "end": v(-86, 37.5) * mm});
            skLineSegment(sketch, "E1056.top", {"start": v(-90, 41.5) * mm, "end": v(-86, 41.5) * mm});
            skLineSegment(sketch, "E1056.left", {"start": v(-90, 37.5) * mm, "end": v(-90, 41.5) * mm});
            skLineSegment(sketch, "E1056.right", {"start": v(-86, 37.5) * mm, "end": v(-86, 41.5) * mm});
            skLineSegment(sketch, "E1057.bottom", {"start": v(-85, 37.5) * mm, "end": v(-81, 37.5) * mm});
            skLineSegment(sketch, "E1057.top", {"start": v(-85, 41.5) * mm, "end": v(-81, 41.5) * mm});
            skLineSegment(sketch, "E1057.left", {"start": v(-85, 37.5) * mm, "end": v(-85, 41.5) * mm});
            skLineSegment(sketch, "E1057.right", {"start": v(-81, 37.5) * mm, "end": v(-81, 41.5) * mm});
            skLineSegment(sketch, "E1058.bottom", {"start": v(-80, 37.5) * mm, "end": v(-76, 37.5) * mm});
            skLineSegment(sketch, "E1058.top", {"start": v(-80, 41.5) * mm, "end": v(-76, 41.5) * mm});
            skLineSegment(sketch, "E1058.left", {"start": v(-80, 37.5) * mm, "end": v(-80, 41.5) * mm});
            skLineSegment(sketch, "E1058.right", {"start": v(-76, 37.5) * mm, "end": v(-76, 41.5) * mm});
            skLineSegment(sketch, "E1059.bottom", {"start": v(-75, 37.5) * mm, "end": v(-71, 37.5) * mm});
            skLineSegment(sketch, "E1059.top", {"start": v(-75, 41.5) * mm, "end": v(-71, 41.5) * mm});
            skLineSegment(sketch, "E1059.left", {"start": v(-75, 37.5) * mm, "end": v(-75, 41.5) * mm});
            skLineSegment(sketch, "E1059.right", {"start": v(-71, 37.5) * mm, "end": v(-71, 41.5) * mm});
            skLineSegment(sketch, "E1060.bottom", {"start": v(-70, 37.5) * mm, "end": v(-66.15, 37.5) * mm});
            skLineSegment(sketch, "E1060.top", {"start": v(-70, 41.5) * mm, "end": v(-66.15, 41.5) * mm});
            skLineSegment(sketch, "E1060.left", {"start": v(-70, 37.5) * mm, "end": v(-70, 41.5) * mm});
            skLineSegment(sketch, "E1060.right", {"start": v(-66.15, 37.5) * mm, "end": v(-66.15, 41.5) * mm});
            skLineSegment(sketch, "E1061.bottom", {"start": v(-65, 37.5) * mm, "end": v(-61, 37.5) * mm});
            skLineSegment(sketch, "E1061.top", {"start": v(-65, 41.5) * mm, "end": v(-61, 41.5) * mm});
            skLineSegment(sketch, "E1061.left", {"start": v(-65, 37.5) * mm, "end": v(-65, 41.5) * mm});
            skLineSegment(sketch, "E1061.right", {"start": v(-61, 37.5) * mm, "end": v(-61, 41.5) * mm});
            skLineSegment(sketch, "E1062.bottom", {"start": v(-60, 37.5) * mm, "end": v(-56, 37.5) * mm});
            skLineSegment(sketch, "E1062.top", {"start": v(-60, 41.5) * mm, "end": v(-56, 41.5) * mm});
            skLineSegment(sketch, "E1062.left", {"start": v(-60, 37.5) * mm, "end": v(-60, 41.5) * mm});
            skLineSegment(sketch, "E1062.right", {"start": v(-56, 37.5) * mm, "end": v(-56, 41.5) * mm});
            skLineSegment(sketch, "E1063.bottom", {"start": v(-55, 37.5) * mm, "end": v(-51, 37.5) * mm});
            skLineSegment(sketch, "E1063.top", {"start": v(-55, 41.5) * mm, "end": v(-51, 41.5) * mm});
            skLineSegment(sketch, "E1063.left", {"start": v(-55, 37.5) * mm, "end": v(-55, 41.5) * mm});
            skLineSegment(sketch, "E1063.right", {"start": v(-51, 37.5) * mm, "end": v(-51, 41.5) * mm});
            skSolve(sketch);
        }
        {
            var Q0;
            Q0=qSketchRegion(id+"F12",true);
            extrude(context, id + "F13", {"entities" : qUnion([Q0]), "operationType" : NewBodyOperationType.REMOVE, "oppositeDirection" : true, "depth" : 5 * mm, "offsetDistance" : 25 * mm});
        }
        {
            var Q0;
            Q0=makeQuery(id+"F5.boolean.opBoolean","MERGE",FACE,{"derivedFrom":[makeQuery(id+"F1.opExtrude","SWEPT_FACE",FACE,{"disambiguationData":[OSD([sQuery(id+"F0.wireOp",EDGE,"E0")])]}),makeQuery(id+"F5.opExtrude","CAP_FACE",FACE,{"disambiguationData":[OSD([sQuery(id+"F4.wireOp",EDGE,"E11"),sQuery(id+"F4.wireOp",EDGE,"E12"),sQuery(id+"F4.wireOp",EDGE,"E13"),sQuery(id+"F4.wireOp",EDGE,"E14")])],"isStart":true})]});
            var sketch = newSketch(context, id + "F14", { "sketchPlane" : qUnion([Q0])});
            skLineSegment(sketch, "E1064", {"start": v(0, 55) * mm, "end": v(120, 55) * mm});
            skLineSegment(sketch, "E1065", {"start": v(120, 55) * mm, "end": v(130, 95) * mm});
            skLineSegment(sketch, "E1066", {"start": v(130, 95) * mm, "end": v(160, 95) * mm});
            skLineSegment(sketch, "E1067", {"start": v(160, 95) * mm, "end": v(160, 0) * mm});
            skLineSegment(sketch, "E1068", {"start": v(160, 0) * mm, "end": v(0, 0) * mm});
            skLineSegment(sketch, "E1069", {"start": v(0, 0) * mm, "end": v(0, 55) * mm});
            skSolve(sketch);
        }
        {
            var Q0;
            Q0=qSketchRegion(id+"F14",true);
            extrude(context, id + "F15", {"entities" : qUnion([Q0]), "operationType" : NewBodyOperationType.ADD, "oppositeDirection" : true, "depth" : 1 * mm, "offsetDistance" : 25 * mm});
        }
        {
            var Q0;
            Q0=makeQuery(id+"F5.boolean.opBoolean","MERGE",FACE,{"derivedFrom":[makeQuery(id+"F1.opExtrude","SWEPT_FACE",FACE,{"disambiguationData":[OSD([sQuery(id+"F0.wireOp",EDGE,"E1")])]}),makeQuery(id+"F5.opExtrude","SWEPT_FACE",FACE,{"disambiguationData":[OSD([sQuery(id+"F4.wireOp",EDGE,"E12")])]})]});
            var sketch = newSketch(context, id + "F16", { "sketchPlane" : qUnion([Q0])});
            skLineSegment(sketch, "E1070", {"start": v(50, 95) * mm, "end": v(50, 0) * mm});
            skCircle(sketch, "E1071", {"center": v(50, 47.5) * mm, "radius": 37.5 * mm});
            skCircle(sketch, "E1072", {"center": v(50, 47.5) * mm, "radius": 37 * mm});
            skCircle(sketch, "E1073", {"center": v(50, 47.5) * mm, "radius": 32.5 * mm});
            skCircle(sketch, "E1074", {"center": v(50, 47.5) * mm, "radius": 32 * mm});
            skCircle(sketch, "E1075", {"center": v(50, 47.5) * mm, "radius": 27.5 * mm});
            skCircle(sketch, "E1076", {"center": v(50, 47.5) * mm, "radius": 27 * mm});
            skCircle(sketch, "E1077", {"center": v(50, 47.5) * mm, "radius": 22.5 * mm});
            skCircle(sketch, "E1078", {"center": v(50, 47.5) * mm, "radius": 22 * mm});
            skCircle(sketch, "E1079", {"center": v(50, 47.5) * mm, "radius": 17.5 * mm});
            skCircle(sketch, "E1080", {"center": v(50, 47.5) * mm, "radius": 17 * mm});
            skCircle(sketch, "E1081", {"center": v(50, 47.5) * mm, "radius": 12.5 * mm});
            skCircle(sketch, "E1082", {"center": v(50, 47.5) * mm, "radius": 12 * mm});
            skCircle(sketch, "E1083", {"center": v(50, 47.5) * mm, "radius": 7.5 * mm});
            skCircle(sketch, "E1084", {"center": v(50, 47.5) * mm, "radius": 7 * mm});
            skCircle(sketch, "E1085", {"center": v(50, 47.5) * mm, "radius": 2.5 * mm});
            skCircle(sketch, "E1086", {"center": v(50, 47.5) * mm, "radius": 3 * mm});
            skCircle(sketch, "E1087", {"center": v(50, 47.5) * mm, "radius": 42.5 * mm});
            skCircle(sketch, "E1088", {"center": v(50, 47.5) * mm, "radius": 42 * mm});
            skSolve(sketch);
        }
        {
            var Q0;
            {var subQ0=sQuery(id+"F16.wireOp",EDGE,"E1071");var subQ1=sQuery(id+"F16.wireOp",EDGE,"E1070");var subQ2=makeQuery(id+"F16.imprint","INTERSECT",VERTEX,{"disambiguationData":[OD(0.0)],"derivedFrom":[subQ1,subQ0]});Q0=makeQuery(id+"F16.imprint","IMPRINT",FACE,{"disambiguationData":[TD([[makeQuery(id+"F16.imprint","IMPRINT",EDGE,{"disambiguationData":[TD([[subQ2,-1.0]])],"derivedFrom":subQ1}),1.0]])]});}
            var Q1;
            {var subQ0=sQuery(id+"F16.wireOp",EDGE,"E1073");var subQ1=sQuery(id+"F16.wireOp",EDGE,"E1070");var subQ2=makeQuery(id+"F16.imprint","INTERSECT",VERTEX,{"disambiguationData":[OD(0.0)],"derivedFrom":[subQ1,subQ0]});Q1=makeQuery(id+"F16.imprint","IMPRINT",FACE,{"disambiguationData":[TD([[makeQuery(id+"F16.imprint","IMPRINT",EDGE,{"disambiguationData":[TD([[subQ2,-1.0]])],"derivedFrom":subQ1}),1.0]])]});}
            var Q2;
            {var subQ0=sQuery(id+"F16.wireOp",EDGE,"E1075");var subQ1=sQuery(id+"F16.wireOp",EDGE,"E1070");var subQ2=makeQuery(id+"F16.imprint","INTERSECT",VERTEX,{"disambiguationData":[OD(0.0)],"derivedFrom":[subQ1,subQ0]});Q2=makeQuery(id+"F16.imprint","IMPRINT",FACE,{"disambiguationData":[TD([[makeQuery(id+"F16.imprint","IMPRINT",EDGE,{"disambiguationData":[TD([[subQ2,-1.0]])],"derivedFrom":subQ1}),1.0]])]});}
            var Q3;
            {var subQ0=sQuery(id+"F16.wireOp",EDGE,"E1077");var subQ1=sQuery(id+"F16.wireOp",EDGE,"E1070");var subQ2=makeQuery(id+"F16.imprint","INTERSECT",VERTEX,{"disambiguationData":[OD(0.0)],"derivedFrom":[subQ1,subQ0]});Q3=makeQuery(id+"F16.imprint","IMPRINT",FACE,{"disambiguationData":[TD([[makeQuery(id+"F16.imprint","IMPRINT",EDGE,{"disambiguationData":[TD([[subQ2,-1.0]])],"derivedFrom":subQ1}),1.0]])]});}
            var Q4;
            {var subQ0=sQuery(id+"F16.wireOp",EDGE,"E1079");var subQ1=sQuery(id+"F16.wireOp",EDGE,"E1070");var subQ2=makeQuery(id+"F16.imprint","INTERSECT",VERTEX,{"disambiguationData":[OD(0.0)],"derivedFrom":[subQ1,subQ0]});Q4=makeQuery(id+"F16.imprint","IMPRINT",FACE,{"disambiguationData":[TD([[makeQuery(id+"F16.imprint","IMPRINT",EDGE,{"disambiguationData":[TD([[subQ2,-1.0]])],"derivedFrom":subQ1}),1.0]])]});}
            var Q5;
            {var subQ0=sQuery(id+"F16.wireOp",EDGE,"E1081");var subQ1=sQuery(id+"F16.wireOp",EDGE,"E1070");var subQ2=makeQuery(id+"F16.imprint","INTERSECT",VERTEX,{"disambiguationData":[OD(0.0)],"derivedFrom":[subQ1,subQ0]});Q5=makeQuery(id+"F16.imprint","IMPRINT",FACE,{"disambiguationData":[TD([[makeQuery(id+"F16.imprint","IMPRINT",EDGE,{"disambiguationData":[TD([[subQ2,-1.0]])],"derivedFrom":subQ1}),1.0]])]});}
            var Q6;
            {var subQ0=sQuery(id+"F16.wireOp",EDGE,"E1083");var subQ1=sQuery(id+"F16.wireOp",EDGE,"E1070");var subQ2=makeQuery(id+"F16.imprint","INTERSECT",VERTEX,{"disambiguationData":[OD(0.0)],"derivedFrom":[subQ1,subQ0]});Q6=makeQuery(id+"F16.imprint","IMPRINT",FACE,{"disambiguationData":[TD([[makeQuery(id+"F16.imprint","IMPRINT",EDGE,{"disambiguationData":[TD([[subQ2,-1.0]])],"derivedFrom":subQ1}),1.0]])]});}
            var Q7;
            {var subQ0=sQuery(id+"F16.wireOp",EDGE,"E1086");var subQ1=sQuery(id+"F16.wireOp",EDGE,"E1070");var subQ2=makeQuery(id+"F16.imprint","INTERSECT",VERTEX,{"disambiguationData":[OD(0.0)],"derivedFrom":[subQ1,subQ0]});Q7=makeQuery(id+"F16.imprint","IMPRINT",FACE,{"disambiguationData":[TD([[makeQuery(id+"F16.imprint","IMPRINT",EDGE,{"disambiguationData":[TD([[subQ2,-1.0]])],"derivedFrom":subQ1}),1.0]])]});}
            var Q8;
            {var subQ0=sQuery(id+"F16.wireOp",EDGE,"E1086");var subQ1=sQuery(id+"F16.wireOp",EDGE,"E1070");var subQ2=makeQuery(id+"F16.imprint","INTERSECT",VERTEX,{"disambiguationData":[OD(0.0)],"derivedFrom":[subQ1,subQ0]});Q8=makeQuery(id+"F16.imprint","IMPRINT",FACE,{"disambiguationData":[TD([[makeQuery(id+"F16.imprint","IMPRINT",EDGE,{"disambiguationData":[TD([[subQ2,-1.0]])],"derivedFrom":subQ1}),-1.0]])]});}
            var Q9;
            {var subQ0=sQuery(id+"F16.wireOp",EDGE,"E1083");var subQ1=sQuery(id+"F16.wireOp",EDGE,"E1070");var subQ2=makeQuery(id+"F16.imprint","INTERSECT",VERTEX,{"disambiguationData":[OD(0.0)],"derivedFrom":[subQ1,subQ0]});Q9=makeQuery(id+"F16.imprint","IMPRINT",FACE,{"disambiguationData":[TD([[makeQuery(id+"F16.imprint","IMPRINT",EDGE,{"disambiguationData":[TD([[subQ2,-1.0]])],"derivedFrom":subQ1}),-1.0]])]});}
            var Q10;
            {var subQ0=sQuery(id+"F16.wireOp",EDGE,"E1081");var subQ1=sQuery(id+"F16.wireOp",EDGE,"E1070");var subQ2=makeQuery(id+"F16.imprint","INTERSECT",VERTEX,{"disambiguationData":[OD(0.0)],"derivedFrom":[subQ1,subQ0]});Q10=makeQuery(id+"F16.imprint","IMPRINT",FACE,{"disambiguationData":[TD([[makeQuery(id+"F16.imprint","IMPRINT",EDGE,{"disambiguationData":[TD([[subQ2,-1.0]])],"derivedFrom":subQ1}),-1.0]])]});}
            var Q11;
            {var subQ0=sQuery(id+"F16.wireOp",EDGE,"E1079");var subQ1=sQuery(id+"F16.wireOp",EDGE,"E1070");var subQ2=makeQuery(id+"F16.imprint","INTERSECT",VERTEX,{"disambiguationData":[OD(0.0)],"derivedFrom":[subQ1,subQ0]});Q11=makeQuery(id+"F16.imprint","IMPRINT",FACE,{"disambiguationData":[TD([[makeQuery(id+"F16.imprint","IMPRINT",EDGE,{"disambiguationData":[TD([[subQ2,-1.0]])],"derivedFrom":subQ1}),-1.0]])]});}
            var Q12;
            {var subQ0=sQuery(id+"F16.wireOp",EDGE,"E1075");var subQ1=sQuery(id+"F16.wireOp",EDGE,"E1070");var subQ2=makeQuery(id+"F16.imprint","INTERSECT",VERTEX,{"disambiguationData":[OD(0.0)],"derivedFrom":[subQ1,subQ0]});Q12=makeQuery(id+"F16.imprint","IMPRINT",FACE,{"disambiguationData":[TD([[makeQuery(id+"F16.imprint","IMPRINT",EDGE,{"disambiguationData":[TD([[subQ2,-1.0]])],"derivedFrom":subQ1}),-1.0]])]});}
            var Q13;
            {var subQ0=sQuery(id+"F16.wireOp",EDGE,"E1077");var subQ1=sQuery(id+"F16.wireOp",EDGE,"E1070");var subQ2=makeQuery(id+"F16.imprint","INTERSECT",VERTEX,{"disambiguationData":[OD(0.0)],"derivedFrom":[subQ1,subQ0]});Q13=makeQuery(id+"F16.imprint","IMPRINT",FACE,{"disambiguationData":[TD([[makeQuery(id+"F16.imprint","IMPRINT",EDGE,{"disambiguationData":[TD([[subQ2,-1.0]])],"derivedFrom":subQ1}),-1.0]])]});}
            var Q14;
            {var subQ0=sQuery(id+"F16.wireOp",EDGE,"E1073");var subQ1=sQuery(id+"F16.wireOp",EDGE,"E1070");var subQ2=makeQuery(id+"F16.imprint","INTERSECT",VERTEX,{"disambiguationData":[OD(0.0)],"derivedFrom":[subQ1,subQ0]});Q14=makeQuery(id+"F16.imprint","IMPRINT",FACE,{"disambiguationData":[TD([[makeQuery(id+"F16.imprint","IMPRINT",EDGE,{"disambiguationData":[TD([[subQ2,-1.0]])],"derivedFrom":subQ1}),-1.0]])]});}
            var Q15;
            {var subQ0=sQuery(id+"F16.wireOp",EDGE,"E1071");var subQ1=sQuery(id+"F16.wireOp",EDGE,"E1070");var subQ2=makeQuery(id+"F16.imprint","INTERSECT",VERTEX,{"disambiguationData":[OD(0.0)],"derivedFrom":[subQ1,subQ0]});Q15=makeQuery(id+"F16.imprint","IMPRINT",FACE,{"disambiguationData":[TD([[makeQuery(id+"F16.imprint","IMPRINT",EDGE,{"disambiguationData":[TD([[subQ2,-1.0]])],"derivedFrom":subQ1}),-1.0]])]});}
            var Q16;
            {var subQ0=sQuery(id+"F16.wireOp",EDGE,"E1087");var subQ1=sQuery(id+"F16.wireOp",EDGE,"E1070");var subQ2=makeQuery(id+"F16.imprint","INTERSECT",VERTEX,{"disambiguationData":[OD(0.0)],"derivedFrom":[subQ1,subQ0]});Q16=makeQuery(id+"F16.imprint","IMPRINT",FACE,{"disambiguationData":[TD([[makeQuery(id+"F16.imprint","IMPRINT",EDGE,{"disambiguationData":[TD([[subQ2,-1.0]])],"derivedFrom":subQ1}),-1.0]])]});}
            var Q17;
            {var subQ0=sQuery(id+"F16.wireOp",EDGE,"E1087");var subQ1=sQuery(id+"F16.wireOp",EDGE,"E1070");var subQ2=makeQuery(id+"F16.imprint","INTERSECT",VERTEX,{"disambiguationData":[OD(0.0)],"derivedFrom":[subQ1,subQ0]});Q17=makeQuery(id+"F16.imprint","IMPRINT",FACE,{"disambiguationData":[TD([[makeQuery(id+"F16.imprint","IMPRINT",EDGE,{"disambiguationData":[TD([[subQ2,-1.0]])],"derivedFrom":subQ1}),1.0]])]});}
            extrude(context, id + "F17", {"entities" : qUnion([Q0, Q1, Q2, Q3, Q4, Q5, Q6, Q7, Q8, Q9, Q10, Q11, Q12, Q13, Q14, Q15, Q16, Q17]), "operationType" : NewBodyOperationType.REMOVE, "oppositeDirection" : true, "depth" : 5 * mm, "offsetDistance" : 25 * mm});
        }
        {
            var Q0;
            Q0=makeQuery(id+"F8.opChamfer","BLEND_FACE",FACE,{"disambiguationData":[OSD([sQuery(id+"F6.wireOp",EDGE,"E15.right")])]});
            var sketch = newSketch(context, id + "F18", { "sketchPlane" : qUnion([Q0])});
            skLineSegment(sketch, "E1089", {"start": v(21.21, 55) * mm, "end": v(18.71, 55) * mm});
            skLineSegment(sketch, "E1090", {"start": v(18.71, 52.5) * mm, "end": v(9.57, 52.5) * mm});
            skLineSegment(sketch, "E1091", {"start": v(9.57, 47.5) * mm, "end": v(9.57, 52.5) * mm});
            skLineSegment(sketch, "E1092", {"start": v(9.57, 47.5) * mm, "end": v(18.71, 47.5) * mm});
            skLineSegment(sketch, "E1093", {"start": v(18.71, 47.5) * mm, "end": v(18.71, 52.5) * mm});
            skPoint(sketch, "E1094.start.orphan", {"position": v(9.57, 55) * mm});
            skPoint(sketch, "E1095.start.orphan", {"position": v(9.57, 45) * mm});
            skSolve(sketch);
        }
        {
            var Q0;
            Q0=qSketchRegion(id+"F18",true);
            extrude(context, id + "F19", {"entities" : qUnion([Q0]), "operationType" : NewBodyOperationType.REMOVE, "oppositeDirection" : true, "depth" : 5 * mm, "offsetDistance" : 25 * mm});
        }
        {
            var Q0;
            {var subQ2=sQuery(id+"F4.wireOp",EDGE,"E12");var subQ4=sQuery(id+"F0.wireOp",EDGE,"E0");var subQ6=sQuery(id+"F0.wireOp",EDGE,"E1");Q0=makeQuery(id+"F17.boolean.opBoolean","SPLIT",FACE,{"disambiguationData":[TD([makeQuery(id+"F1.opExtrude","SWEPT_FACE",FACE,{"disambiguationData":[OSD([subQ4])]})])],"derivedFrom":makeQuery(id+"F5.boolean.opBoolean","MERGE",FACE,{"derivedFrom":[makeQuery(id+"F1.opExtrude","SWEPT_FACE",FACE,{"disambiguationData":[OSD([subQ6])]}),makeQuery(id+"F5.opExtrude","SWEPT_FACE",FACE,{"disambiguationData":[OSD([subQ2])]})]})});}
            var sketch = newSketch(context, id + "F20", { "sketchPlane" : qUnion([Q0])});
            skLineSegment(sketch, "E1096.bottom", {"start": v(50, 95) * mm, "end": v(49, 95) * mm});
            skLineSegment(sketch, "E1096.top", {"start": v(50, 0) * mm, "end": v(49, 0) * mm});
            skLineSegment(sketch, "E1096.left", {"start": v(50, 95) * mm, "end": v(50, 0) * mm});
            skLineSegment(sketch, "E1096.right", {"start": v(49, 95) * mm, "end": v(49, 0) * mm});
            skSolve(sketch);
        }
        {
            var Q0;
            Q0=qSketchRegion(id+"F20",true);
            extrude(context, id + "F21", {"entities" : qUnion([Q0]), "operationType" : NewBodyOperationType.ADD, "oppositeDirection" : true, "depth" : 2 * mm, "offsetDistance" : 25 * mm});
        }
    });
